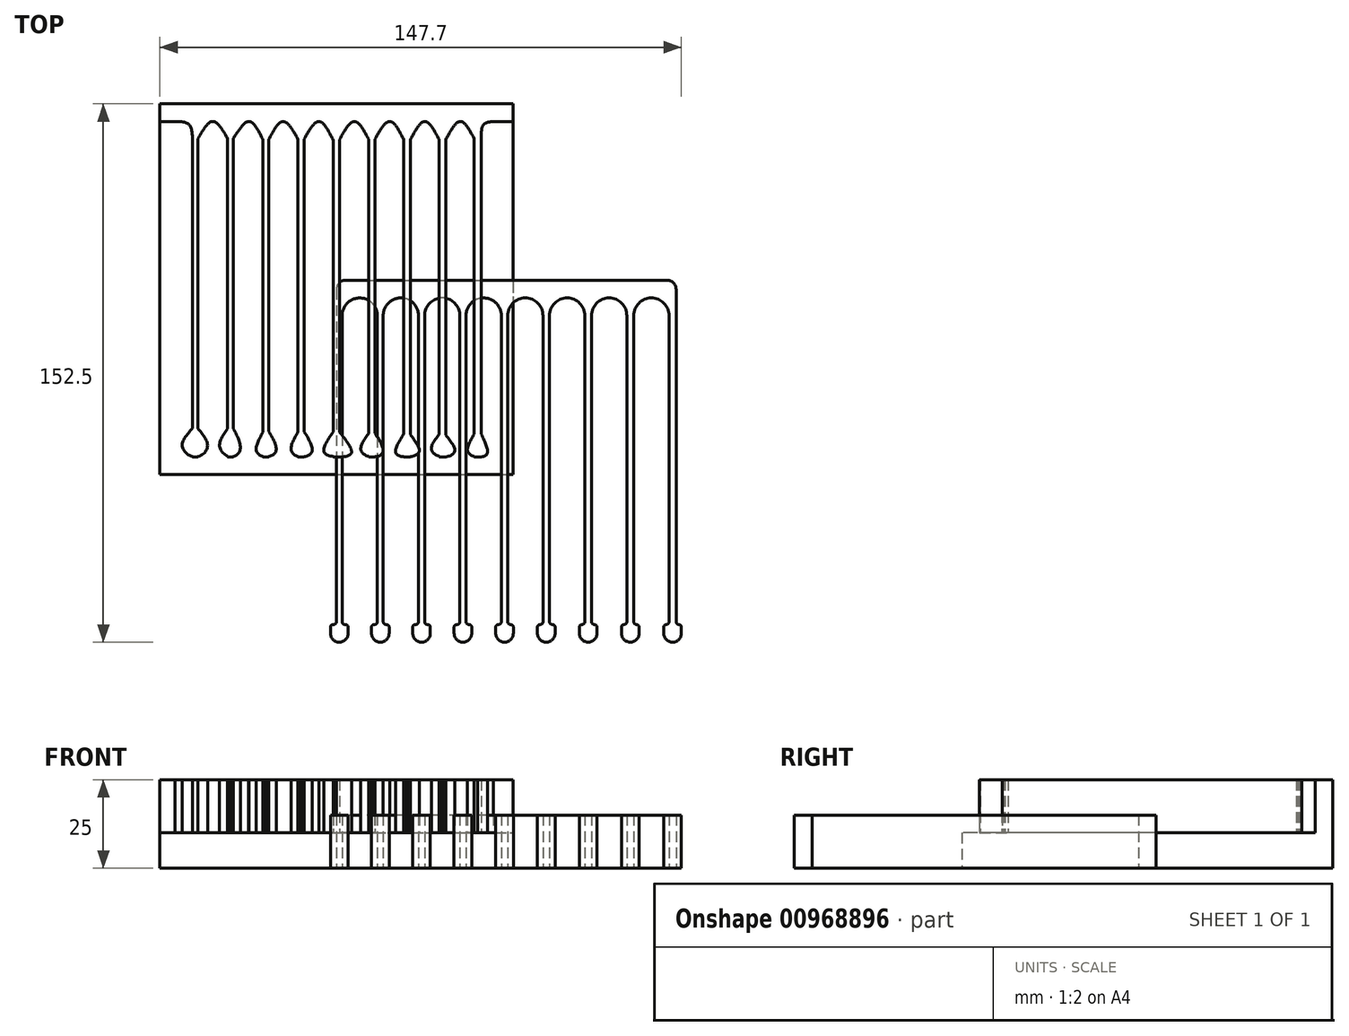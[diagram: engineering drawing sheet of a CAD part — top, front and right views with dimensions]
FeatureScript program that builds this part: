
annotation { "Feature Type Name" : "Feature", "Feature Type Description" : "" }
export const myFeature = defineFeature(function(context is Context, id is Id, definition is map)
    precondition{}
    {
        {
            var Q0;
            Q0=qCreatedBy(makeId("Top.planeOp"),FACE);
            var sketch = newSketch(context, id + "F0", { "sketchPlane" : qUnion([Q0])});
            skLineSegment(sketch, "E0.bottom", {"start": v(-50, 50) * mm, "end": v(50, 50) * mm});
            skLineSegment(sketch, "E0.top", {"start": v(-50, -50) * mm, "end": v(50, -50) * mm});
            skPoint(sketch, "E0.middle", {"position": v(0, 0) * mm});
            skLineSegment(sketch, "E1", {"start": v(-131.96, 0) * mm, "end": v(145.8, 0) * mm});
            skLineSegment(sketch, "E2.bottom", {"start": v(-0.9, 50) * mm, "end": v(0.9, 50) * mm});
            skLineSegment(sketch, "E2.top", {"start": v(-0.9, -50) * mm, "end": v(0.9, -50) * mm});
            skLineSegment(sketch, "E2.left", {"start": v(-0.9, 50) * mm, "end": v(-0.9, -50) * mm});
            skLineSegment(sketch, "E2.right", {"start": v(0.9, 50) * mm, "end": v(0.9, -50) * mm});
            skLineSegment(sketch, "E3", {"start": v(0, 0) * mm, "end": v(10, 0) * mm});
            skLineSegment(sketch, "E4", {"start": v(10, 0) * mm, "end": v(20, 0) * mm});
            skLineSegment(sketch, "E5", {"start": v(20, 0) * mm, "end": v(30, 0) * mm});
            skLineSegment(sketch, "E6", {"start": v(30, 0) * mm, "end": v(40, 0) * mm});
            skLineSegment(sketch, "E7", {"start": v(0, 86.17) * mm, "end": v(0, -73.16) * mm});
            skLineSegment(sketch, "E8.bottom", {"start": v(9.08, 50) * mm, "end": v(10.93, 50) * mm});
            skLineSegment(sketch, "E8.top", {"start": v(9.08, -50) * mm, "end": v(10.93, -50) * mm});
            skLineSegment(sketch, "E8.left", {"start": v(9.08, 50) * mm, "end": v(9.08, -50) * mm});
            skLineSegment(sketch, "E8.right", {"start": v(10.93, 50) * mm, "end": v(10.93, -50) * mm});
            skPoint(sketch, "E8.middle", {"position": v(10, 0) * mm});
            skLineSegment(sketch, "E9.bottom", {"start": v(19.05, 50) * mm, "end": v(20.95, 50) * mm});
            skLineSegment(sketch, "E9.top", {"start": v(19.05, -50) * mm, "end": v(20.95, -50) * mm});
            skLineSegment(sketch, "E9.left", {"start": v(19.05, 50) * mm, "end": v(19.05, -50) * mm});
            skLineSegment(sketch, "E9.right", {"start": v(20.95, 50) * mm, "end": v(20.95, -50) * mm});
            skPoint(sketch, "E9.middle", {"position": v(20, 0) * mm});
            skLineSegment(sketch, "E10.bottom", {"start": v(29.02, 50) * mm, "end": v(30.97, 50) * mm});
            skLineSegment(sketch, "E10.top", {"start": v(29.02, -50) * mm, "end": v(30.97, -50) * mm});
            skLineSegment(sketch, "E10.left", {"start": v(29.02, 50) * mm, "end": v(29.02, -50) * mm});
            skLineSegment(sketch, "E10.right", {"start": v(30.97, 50) * mm, "end": v(30.97, -50) * mm});
            skPoint(sketch, "E10.middle", {"position": v(30, 0) * mm});
            skLineSegment(sketch, "E11.bottom", {"start": v(39, 50) * mm, "end": v(41, 50) * mm});
            skLineSegment(sketch, "E11.top", {"start": v(39, -50) * mm, "end": v(41, -50) * mm});
            skLineSegment(sketch, "E11.left", {"start": v(39, 50) * mm, "end": v(39, -50) * mm});
            skLineSegment(sketch, "E11.right", {"start": v(41, 50) * mm, "end": v(41, -50) * mm});
            skPoint(sketch, "E11.middle", {"position": v(40, 0) * mm});
            skLineSegment(sketch, "E12", {"start": v(0, 0) * mm, "end": v(-10, 0) * mm});
            skLineSegment(sketch, "E13", {"start": v(-10, 0) * mm, "end": v(-20, 0) * mm});
            skLineSegment(sketch, "E14", {"start": v(-20, 0) * mm, "end": v(-30, 0) * mm});
            skLineSegment(sketch, "E15", {"start": v(-30, 0) * mm, "end": v(-40, 0) * mm});
            skLineSegment(sketch, "E16.bottom", {"start": v(-10.88, 50) * mm, "end": v(-9.13, 50) * mm});
            skLineSegment(sketch, "E16.top", {"start": v(-10.88, -50) * mm, "end": v(-9.13, -50) * mm});
            skLineSegment(sketch, "E16.left", {"start": v(-10.88, 50) * mm, "end": v(-10.88, -50) * mm});
            skLineSegment(sketch, "E16.right", {"start": v(-9.13, 50) * mm, "end": v(-9.13, -50) * mm});
            skPoint(sketch, "E16.middle", {"position": v(-10, 0) * mm});
            skLineSegment(sketch, "E17.bottom", {"start": v(-20.85, 50) * mm, "end": v(-19.15, 50) * mm});
            skLineSegment(sketch, "E17.top", {"start": v(-20.85, -50) * mm, "end": v(-19.15, -50) * mm});
            skLineSegment(sketch, "E17.left", {"start": v(-20.85, 50) * mm, "end": v(-20.85, -50) * mm});
            skLineSegment(sketch, "E17.right", {"start": v(-19.15, 50) * mm, "end": v(-19.15, -50) * mm});
            skPoint(sketch, "E17.middle", {"position": v(-20, 0) * mm});
            skLineSegment(sketch, "E18.bottom", {"start": v(-30.83, 50) * mm, "end": v(-29.18, 50) * mm});
            skLineSegment(sketch, "E18.top", {"start": v(-30.83, -50) * mm, "end": v(-29.18, -50) * mm});
            skLineSegment(sketch, "E18.left", {"start": v(-30.83, 50) * mm, "end": v(-30.83, -50) * mm});
            skLineSegment(sketch, "E18.right", {"start": v(-29.18, 50) * mm, "end": v(-29.18, -50) * mm});
            skPoint(sketch, "E18.middle", {"position": v(-30, 0) * mm});
            skLineSegment(sketch, "E19.bottom", {"start": v(-40.8, 50) * mm, "end": v(-39.2, 50) * mm});
            skLineSegment(sketch, "E19.top", {"start": v(-40.8, -50) * mm, "end": v(-39.2, -50) * mm});
            skLineSegment(sketch, "E19.left", {"start": v(-40.8, 50) * mm, "end": v(-40.8, -50) * mm});
            skLineSegment(sketch, "E19.right", {"start": v(-39.2, 50) * mm, "end": v(-39.2, -50) * mm});
            skPoint(sketch, "E19.middle", {"position": v(-40, 0) * mm});
            skLineSegment(sketch, "E20", {"start": v(40, 0) * mm, "end": v(50, 0) * mm});
            skLineSegment(sketch, "E21", {"start": v(-40, 0) * mm, "end": v(-50, 0) * mm});
            skLineSegment(sketch, "E22", {"start": v(-50, 50) * mm, "end": v(-50, -50) * mm});
            skLineSegment(sketch, "E23", {"start": v(50, 50) * mm, "end": v(50, -50) * mm});
            skPoint(sketch, "E24.orphan", {"position": v(100, 50) * mm});
            skPoint(sketch, "E25.orphan", {"position": v(100, -50) * mm});
            skPoint(sketch, "E26.orphan", {"position": v(-100, -50) * mm});
            skPoint(sketch, "E27.orphan", {"position": v(-100, 50) * mm});
            skLineSegment(sketch, "E28", {"start": v(-50, 50) * mm, "end": v(-50, 45) * mm});
            skLineSegment(sketch, "E29", {"start": v(-50, 45) * mm, "end": v(50, 45) * mm});
            skFitSpline(sketch, "E30", {"points": [v(-39.2, 40.14) * mm, v(-35.05, 45) * mm, v(-30.83, 40.15) * mm], "startDerivative": vector(8.28, 14.59) * mm, "endDerivative": vector(8.47, -14.54) * mm});
            skFitSpline(sketch, "E31", {"points": [v(-29.18, 40.2) * mm, v(-24.72, 45) * mm, v(-20.85, 39.83) * mm], "startDerivative": vector(9.17, 14.56) * mm, "endDerivative": vector(7.48, -15.35) * mm});
            skFitSpline(sketch, "E32", {"points": [v(-19.15, 39.93) * mm, v(-15.11, 45) * mm, v(-10.88, 39.9) * mm], "startDerivative": vector(8.05, 15.26) * mm, "endDerivative": vector(8.5, -15.27) * mm});
            skFitSpline(sketch, "E33", {"points": [v(-9.13, 40.03) * mm, v(-4.96, 45) * mm, v(-0.9, 39.67) * mm], "startDerivative": vector(8.48, 15.14) * mm, "endDerivative": vector(7.98, -15.77) * mm});
            skFitSpline(sketch, "E34", {"points": [v(0.9, 39.88) * mm, v(5.1, 45) * mm, v(9.08, 40) * mm], "startDerivative": vector(8.4, 15.25) * mm, "endDerivative": vector(7.96, -15.1) * mm});
            skFitSpline(sketch, "E35", {"points": [v(10.93, 40.04) * mm, v(15.1, 45) * mm, v(19.05, 39.86) * mm], "startDerivative": vector(8.49, 14.96) * mm, "endDerivative": vector(7.76, -15.32) * mm});
            skFitSpline(sketch, "E36", {"points": [v(20.95, 39.83) * mm, v(25.05, 45) * mm, v(29.02, 39.93) * mm], "startDerivative": vector(8.18, 15.43) * mm, "endDerivative": vector(7.97, -15.3) * mm});
            skFitSpline(sketch, "E37", {"points": [v(30.97, 39.85) * mm, v(35.1, 45) * mm, v(39, 40.14) * mm], "startDerivative": vector(8.18, 15.23) * mm, "endDerivative": vector(7.87, -14.8) * mm});
            skFitSpline(sketch, "E38", {"points": [v(-45.79, 45) * mm, v(-41.8, 44.16) * mm, v(-40.8, 40.58) * mm], "startDerivative": vector(9.28, -0.19) * mm, "endDerivative": vector(0.63, -8.72) * mm});
            skFitSpline(sketch, "E39", {"points": [v(41, 40.1) * mm, v(41.67, 44.1) * mm, v(44.48, 45) * mm], "startDerivative": vector(-0.07, 8.9) * mm, "endDerivative": vector(7.22, 0.69) * mm});
            skFitSpline(sketch, "E40", {"points": [v(-40.8, -41.94) * mm, v(-43.65, -47.12) * mm, v(-40, -50) * mm, v(-36.55, -47.26) * mm, v(-39.2, -42.01) * mm], "startDerivative": vector(-17.63, -19.78) * mm, "endDerivative": vector(-16.6, 20.3) * mm});
            skFitSpline(sketch, "E41", {"points": [v(-30.83, -42.01) * mm, v(-33.07, -47.2) * mm, v(-30, -50) * mm, v(-27.32, -48.12) * mm, v(-29.18, -42.01) * mm], "startDerivative": vector(-14.12, -19.61) * mm, "endDerivative": vector(-11.98, 23.35) * mm});
            skFitSpline(sketch, "E42", {"points": [v(-20.85, -43.08) * mm, v(-22.64, -48.4) * mm, v(-20, -50) * mm, v(-17.17, -48.47) * mm, v(-19.15, -42.8) * mm], "startDerivative": vector(-11.66, -21.24) * mm, "endDerivative": vector(-12.59, 22.12) * mm});
            skFitSpline(sketch, "E43", {"points": [v(-10.88, -42.86) * mm, v(-12.77, -48.33) * mm, v(-10, -50) * mm, v(-6.95, -48.61) * mm, v(-9.13, -42.93) * mm], "startDerivative": vector(-12.25, -21.86) * mm, "endDerivative": vector(-13.83, 22.6) * mm});
            skFitSpline(sketch, "E44", {"points": [v(-0.9, -42.92) * mm, v(-3.55, -48.54) * mm, v(0, -50) * mm, v(4.18, -49) * mm, v(0.9, -43.02) * mm], "startDerivative": vector(-16.86, -24.11) * mm, "endDerivative": vector(-20.02, 25.12) * mm});
            skFitSpline(sketch, "E45", {"points": [v(9.08, -43.42) * mm, v(6.94, -48.19) * mm, v(10, -50) * mm, v(13.16, -48.7) * mm, v(10.93, -43.32) * mm], "startDerivative": vector(-13.73, -19.48) * mm, "endDerivative": vector(-14.17, 21.68) * mm});
            skFitSpline(sketch, "E46", {"points": [v(19.05, -43.47) * mm, v(16.83, -48.94) * mm, v(20, -50) * mm, v(23.4, -48.7) * mm, v(20.95, -43.67) * mm], "startDerivative": vector(-14.18, -22.89) * mm, "endDerivative": vector(-15.57, 21.12) * mm});
            skFitSpline(sketch, "E47", {"points": [v(29.02, -43.67) * mm, v(26.91, -47.99) * mm, v(30, -50) * mm, v(33.44, -48.6) * mm, v(30.97, -43.77) * mm], "startDerivative": vector(-13.65, -17.73) * mm, "endDerivative": vector(-15.5, 19.57) * mm});
            skFitSpline(sketch, "E48", {"points": [v(39, -43.57) * mm, v(37.2, -48.54) * mm, v(40, -50) * mm, v(42.67, -49.14) * mm, v(41, -43.57) * mm], "startDerivative": vector(-11.82, -20.28) * mm, "endDerivative": vector(-11.16, 22.74) * mm});
            skLineSegment(sketch, "E49.bottom", {"start": v(50, -50) * mm, "end": v(-50, -50) * mm});
            skLineSegment(sketch, "E49.top", {"start": v(50, -55) * mm, "end": v(-50, -55) * mm});
            skLineSegment(sketch, "E49.left", {"start": v(50, -50) * mm, "end": v(50, -55) * mm});
            skLineSegment(sketch, "E49.right", {"start": v(-50, -50) * mm, "end": v(-50, -55) * mm});
            skSolve(sketch);
        }
        {
            var Q0;
            {var subQ4=sQuery(id+"F0.wireOp",EDGE,"E22");var subQ5=sQuery(id+"F0.wireOp",EDGE,"E0.bottom");var subQ6=makeQuery(id+"F0.imprint","INTERSECT",VERTEX,{"derivedFrom":[subQ5,subQ4]});Q0=makeQuery(id+"F0.imprint","IMPRINT",FACE,{"disambiguationData":[TD([[makeQuery(id+"F0.imprint","IMPRINT",EDGE,{"disambiguationData":[TD([[subQ6,-1.0]])],"derivedFrom":subQ5}),-1.0]])]});}
            var Q1;
            {var subQ0=sQuery(id+"F0.wireOp",EDGE,"E11.right");var subQ1=sQuery(id+"F0.wireOp",EDGE,"E0.bottom");var subQ2=makeQuery(id+"F0.imprint","INTERSECT",VERTEX,{"derivedFrom":[subQ1,subQ0]});Q1=makeQuery(id+"F0.imprint","IMPRINT",FACE,{"disambiguationData":[TD([[makeQuery(id+"F0.imprint","IMPRINT",EDGE,{"disambiguationData":[TD([[subQ2,1.0]])],"derivedFrom":subQ1}),-1.0]])]});}
            var Q2;
            {var subQ4=sQuery(id+"F0.wireOp",EDGE,"E0.bottom");var subQ6=sQuery(id+"F0.wireOp",EDGE,"E11.left");var subQ7=makeQuery(id+"F0.imprint","INTERSECT",VERTEX,{"derivedFrom":[subQ4,subQ6]});Q2=makeQuery(id+"F0.imprint","IMPRINT",FACE,{"disambiguationData":[TD([[makeQuery(id+"F0.imprint","IMPRINT",EDGE,{"disambiguationData":[TD([[subQ7,1.0]])],"derivedFrom":subQ4}),-1.0]])]});}
            var Q3;
            {var subQ0=sQuery(id+"F0.wireOp",EDGE,"E2.left");var subQ1=sQuery(id+"F0.wireOp",EDGE,"E0.bottom");var subQ2=makeQuery(id+"F0.imprint","INTERSECT",VERTEX,{"derivedFrom":[subQ1,subQ0]});Q3=makeQuery(id+"F0.imprint","IMPRINT",FACE,{"disambiguationData":[TD([[makeQuery(id+"F0.imprint","IMPRINT",EDGE,{"disambiguationData":[TD([[subQ2,-1.0]])],"derivedFrom":subQ1}),-1.0]])]});}
            var Q4;
            {var subQ0=sQuery(id+"F0.wireOp",EDGE,"E8.left");var subQ1=sQuery(id+"F0.wireOp",EDGE,"E0.bottom");var subQ2=makeQuery(id+"F0.imprint","INTERSECT",VERTEX,{"derivedFrom":[subQ1,subQ0]});Q4=makeQuery(id+"F0.imprint","IMPRINT",FACE,{"disambiguationData":[TD([[makeQuery(id+"F0.imprint","IMPRINT",EDGE,{"disambiguationData":[TD([[subQ2,-1.0]])],"derivedFrom":subQ1}),-1.0]])]});}
            var Q5;
            {var subQ0=sQuery(id+"F0.wireOp",EDGE,"E10.left");var subQ1=sQuery(id+"F0.wireOp",EDGE,"E0.bottom");var subQ2=makeQuery(id+"F0.imprint","INTERSECT",VERTEX,{"derivedFrom":[subQ1,subQ0]});Q5=makeQuery(id+"F0.imprint","IMPRINT",FACE,{"disambiguationData":[TD([[makeQuery(id+"F0.imprint","IMPRINT",EDGE,{"disambiguationData":[TD([[subQ2,-1.0]])],"derivedFrom":subQ1}),-1.0]])]});}
            var Q6;
            {var subQ1=sQuery(id+"F0.wireOp",EDGE,"E0.bottom");var subQ7=sQuery(id+"F0.wireOp",EDGE,"E17.left");var subQ8=makeQuery(id+"F0.imprint","INTERSECT",VERTEX,{"derivedFrom":[subQ1,subQ7]});Q6=makeQuery(id+"F0.imprint","IMPRINT",FACE,{"disambiguationData":[TD([[makeQuery(id+"F0.imprint","IMPRINT",EDGE,{"disambiguationData":[TD([[subQ8,1.0]])],"derivedFrom":subQ1}),-1.0]])]});}
            var Q7;
            {var subQ0=sQuery(id+"F0.wireOp",EDGE,"E16.left");var subQ1=sQuery(id+"F0.wireOp",EDGE,"E0.bottom");var subQ2=makeQuery(id+"F0.imprint","INTERSECT",VERTEX,{"derivedFrom":[subQ1,subQ0]});Q7=makeQuery(id+"F0.imprint","IMPRINT",FACE,{"disambiguationData":[TD([[makeQuery(id+"F0.imprint","IMPRINT",EDGE,{"disambiguationData":[TD([[subQ2,1.0]])],"derivedFrom":subQ1}),-1.0]])]});}
            var Q8;
            {var subQ3=sQuery(id+"F0.wireOp",EDGE,"E18.left");var subQ5=sQuery(id+"F0.wireOp",EDGE,"E0.bottom");var subQ6=makeQuery(id+"F0.imprint","INTERSECT",VERTEX,{"derivedFrom":[subQ5,subQ3]});Q8=makeQuery(id+"F0.imprint","IMPRINT",FACE,{"disambiguationData":[TD([[makeQuery(id+"F0.imprint","IMPRINT",EDGE,{"disambiguationData":[TD([[subQ6,1.0]])],"derivedFrom":subQ5}),-1.0]])]});}
            var Q9;
            {var subQ0=sQuery(id+"F0.wireOp",EDGE,"E9.left");var subQ1=sQuery(id+"F0.wireOp",EDGE,"E0.bottom");var subQ2=makeQuery(id+"F0.imprint","INTERSECT",VERTEX,{"derivedFrom":[subQ1,subQ0]});Q9=makeQuery(id+"F0.imprint","IMPRINT",FACE,{"disambiguationData":[TD([[makeQuery(id+"F0.imprint","IMPRINT",EDGE,{"disambiguationData":[TD([[subQ2,-1.0]])],"derivedFrom":subQ1}),-1.0]])]});}
            var Q10;
            {var subQ1=sQuery(id+"F0.wireOp",EDGE,"E2.right");var subQ6=sQuery(id+"F0.wireOp",EDGE,"E0.bottom");var subQ9=makeQuery(id+"F0.imprint","INTERSECT",VERTEX,{"derivedFrom":[subQ6,subQ1]});Q10=makeQuery(id+"F0.imprint","IMPRINT",FACE,{"disambiguationData":[TD([[makeQuery(id+"F0.imprint","IMPRINT",EDGE,{"disambiguationData":[TD([[subQ9,-1.0]])],"derivedFrom":subQ6}),-1.0]])]});}
            var Q11;
            {var subQ0=sQuery(id+"F0.wireOp",EDGE,"E16.left");var subQ1=sQuery(id+"F0.wireOp",EDGE,"E0.bottom");var subQ2=makeQuery(id+"F0.imprint","INTERSECT",VERTEX,{"derivedFrom":[subQ1,subQ0]});Q11=makeQuery(id+"F0.imprint","IMPRINT",FACE,{"disambiguationData":[TD([[makeQuery(id+"F0.imprint","IMPRINT",EDGE,{"disambiguationData":[TD([[subQ2,-1.0]])],"derivedFrom":subQ1}),-1.0]])]});}
            var Q12;
            {var subQ1=sQuery(id+"F0.wireOp",EDGE,"E16.right");var subQ5=sQuery(id+"F0.wireOp",EDGE,"E0.bottom");var subQ6=makeQuery(id+"F0.imprint","INTERSECT",VERTEX,{"derivedFrom":[subQ5,subQ1]});Q12=makeQuery(id+"F0.imprint","IMPRINT",FACE,{"disambiguationData":[TD([[makeQuery(id+"F0.imprint","IMPRINT",EDGE,{"disambiguationData":[TD([[subQ6,-1.0]])],"derivedFrom":subQ5}),-1.0]])]});}
            var Q13;
            {var subQ4=sQuery(id+"F0.wireOp",EDGE,"E10.left");var subQ5=sQuery(id+"F0.wireOp",EDGE,"E0.bottom");var subQ6=makeQuery(id+"F0.imprint","INTERSECT",VERTEX,{"derivedFrom":[subQ5,subQ4]});Q13=makeQuery(id+"F0.imprint","IMPRINT",FACE,{"disambiguationData":[TD([[makeQuery(id+"F0.imprint","IMPRINT",EDGE,{"disambiguationData":[TD([[subQ6,1.0]])],"derivedFrom":subQ5}),-1.0]])]});}
            var Q14;
            {var subQ1=sQuery(id+"F0.wireOp",EDGE,"E23");var subQ3=sQuery(id+"F0.wireOp",EDGE,"E0.bottom");var subQ4=makeQuery(id+"F0.imprint","INTERSECT",VERTEX,{"derivedFrom":[subQ3,subQ1]});Q14=makeQuery(id+"F0.imprint","IMPRINT",FACE,{"disambiguationData":[TD([[makeQuery(id+"F0.imprint","IMPRINT",EDGE,{"disambiguationData":[TD([[subQ4,1.0]])],"derivedFrom":subQ3}),-1.0]])]});}
            var Q15;
            {var subQ0=sQuery(id+"F0.wireOp",EDGE,"E19.left");var subQ1=sQuery(id+"F0.wireOp",EDGE,"E0.bottom");var subQ2=makeQuery(id+"F0.imprint","INTERSECT",VERTEX,{"derivedFrom":[subQ1,subQ0]});Q15=makeQuery(id+"F0.imprint","IMPRINT",FACE,{"disambiguationData":[TD([[makeQuery(id+"F0.imprint","IMPRINT",EDGE,{"disambiguationData":[TD([[subQ2,-1.0]])],"derivedFrom":subQ1}),-1.0]])]});}
            var Q16;
            {var subQ5=sQuery(id+"F0.wireOp",EDGE,"E9.left");var subQ6=sQuery(id+"F0.wireOp",EDGE,"E0.bottom");var subQ7=makeQuery(id+"F0.imprint","INTERSECT",VERTEX,{"derivedFrom":[subQ6,subQ5]});Q16=makeQuery(id+"F0.imprint","IMPRINT",FACE,{"disambiguationData":[TD([[makeQuery(id+"F0.imprint","IMPRINT",EDGE,{"disambiguationData":[TD([[subQ7,1.0]])],"derivedFrom":subQ6}),-1.0]])]});}
            var Q17;
            {var subQ0=sQuery(id+"F0.wireOp",EDGE,"E2.right");var subQ1=sQuery(id+"F0.wireOp",EDGE,"E0.bottom");var subQ2=makeQuery(id+"F0.imprint","INTERSECT",VERTEX,{"derivedFrom":[subQ1,subQ0]});Q17=makeQuery(id+"F0.imprint","IMPRINT",FACE,{"disambiguationData":[TD([[makeQuery(id+"F0.imprint","IMPRINT",EDGE,{"disambiguationData":[TD([[subQ2,1.0]])],"derivedFrom":subQ1}),-1.0]])]});}
            var Q18;
            {var subQ0=sQuery(id+"F0.wireOp",EDGE,"E17.left");var subQ1=sQuery(id+"F0.wireOp",EDGE,"E0.bottom");var subQ2=makeQuery(id+"F0.imprint","INTERSECT",VERTEX,{"derivedFrom":[subQ1,subQ0]});Q18=makeQuery(id+"F0.imprint","IMPRINT",FACE,{"disambiguationData":[TD([[makeQuery(id+"F0.imprint","IMPRINT",EDGE,{"disambiguationData":[TD([[subQ2,-1.0]])],"derivedFrom":subQ1}),-1.0]])]});}
            var Q19;
            {var subQ0=sQuery(id+"F0.wireOp",EDGE,"E18.left");var subQ1=sQuery(id+"F0.wireOp",EDGE,"E0.bottom");var subQ2=makeQuery(id+"F0.imprint","INTERSECT",VERTEX,{"derivedFrom":[subQ1,subQ0]});Q19=makeQuery(id+"F0.imprint","IMPRINT",FACE,{"disambiguationData":[TD([[makeQuery(id+"F0.imprint","IMPRINT",EDGE,{"disambiguationData":[TD([[subQ2,-1.0]])],"derivedFrom":subQ1}),-1.0]])]});}
            var Q20;
            {var subQ0=sQuery(id+"F0.wireOp",EDGE,"E33");var subQ1=sQuery(id+"F0.wireOp",EDGE,"E29");var subQ2=makeQuery(id+"F0.imprint","INTERSECT",VERTEX,{"disambiguationData":[OD(0.0)],"derivedFrom":[subQ1,subQ0]});Q20=makeQuery(id+"F0.imprint","IMPRINT",FACE,{"disambiguationData":[TD([[makeQuery(id+"F0.imprint","IMPRINT",EDGE,{"disambiguationData":[TD([[subQ2,-1.0]])],"derivedFrom":subQ1}),1.0]])]});}
            var Q21;
            {var subQ0=sQuery(id+"F0.wireOp",EDGE,"E31");var subQ1=sQuery(id+"F0.wireOp",EDGE,"E29");var subQ2=makeQuery(id+"F0.imprint","INTERSECT",VERTEX,{"disambiguationData":[OD(0.0)],"derivedFrom":[subQ1,subQ0]});Q21=makeQuery(id+"F0.imprint","IMPRINT",FACE,{"disambiguationData":[TD([[makeQuery(id+"F0.imprint","IMPRINT",EDGE,{"disambiguationData":[TD([[subQ2,-1.0]])],"derivedFrom":subQ1}),1.0]])]});}
            var Q22;
            {var subQ0=sQuery(id+"F0.wireOp",EDGE,"E35");var subQ1=sQuery(id+"F0.wireOp",EDGE,"E29");var subQ2=makeQuery(id+"F0.imprint","INTERSECT",VERTEX,{"disambiguationData":[OD(0.0)],"derivedFrom":[subQ1,subQ0]});Q22=makeQuery(id+"F0.imprint","IMPRINT",FACE,{"disambiguationData":[TD([[makeQuery(id+"F0.imprint","IMPRINT",EDGE,{"disambiguationData":[TD([[subQ2,-1.0]])],"derivedFrom":subQ1}),1.0]])]});}
            var Q23;
            {var subQ0=sQuery(id+"F0.wireOp",EDGE,"E32");var subQ1=sQuery(id+"F0.wireOp",EDGE,"E17.right");var subQ2=makeQuery(id+"F0.imprint","INTERSECT",VERTEX,{"derivedFrom":[subQ1,subQ0]});Q23=makeQuery(id+"F0.imprint","IMPRINT",FACE,{"disambiguationData":[TD([[makeQuery(id+"F0.imprint","IMPRINT",EDGE,{"disambiguationData":[TD([[subQ2,1.0]])],"derivedFrom":subQ1}),1.0]])]});}
            var Q24;
            {var subQ0=sQuery(id+"F0.wireOp",EDGE,"E31");var subQ1=sQuery(id+"F0.wireOp",EDGE,"E18.right");var subQ2=makeQuery(id+"F0.imprint","INTERSECT",VERTEX,{"derivedFrom":[subQ1,subQ0]});Q24=makeQuery(id+"F0.imprint","IMPRINT",FACE,{"disambiguationData":[TD([[makeQuery(id+"F0.imprint","IMPRINT",EDGE,{"disambiguationData":[TD([[subQ2,1.0]])],"derivedFrom":subQ1}),1.0]])]});}
            var Q25;
            {var subQ0=sQuery(id+"F0.wireOp",EDGE,"E35");var subQ1=sQuery(id+"F0.wireOp",EDGE,"E9.left");var subQ2=makeQuery(id+"F0.imprint","INTERSECT",VERTEX,{"derivedFrom":[subQ1,subQ0]});Q25=makeQuery(id+"F0.imprint","IMPRINT",FACE,{"disambiguationData":[TD([[makeQuery(id+"F0.imprint","IMPRINT",EDGE,{"disambiguationData":[TD([[subQ2,1.0]])],"derivedFrom":subQ1}),-1.0]])]});}
            var Q26;
            {var subQ0=sQuery(id+"F0.wireOp",EDGE,"E30");var subQ1=sQuery(id+"F0.wireOp",EDGE,"E18.left");var subQ2=makeQuery(id+"F0.imprint","INTERSECT",VERTEX,{"derivedFrom":[subQ1,subQ0]});Q26=makeQuery(id+"F0.imprint","IMPRINT",FACE,{"disambiguationData":[TD([[makeQuery(id+"F0.imprint","IMPRINT",EDGE,{"disambiguationData":[TD([[subQ2,1.0]])],"derivedFrom":subQ1}),-1.0]])]});}
            var Q27;
            {var subQ0=sQuery(id+"F0.wireOp",EDGE,"E33");var subQ1=sQuery(id+"F0.wireOp",EDGE,"E2.left");var subQ2=makeQuery(id+"F0.imprint","INTERSECT",VERTEX,{"derivedFrom":[subQ1,subQ0]});Q27=makeQuery(id+"F0.imprint","IMPRINT",FACE,{"disambiguationData":[TD([[makeQuery(id+"F0.imprint","IMPRINT",EDGE,{"disambiguationData":[TD([[subQ2,1.0]])],"derivedFrom":subQ1}),-1.0]])]});}
            var Q28;
            {var subQ0=sQuery(id+"F0.wireOp",EDGE,"E37");var subQ1=sQuery(id+"F0.wireOp",EDGE,"E11.left");var subQ2=makeQuery(id+"F0.imprint","INTERSECT",VERTEX,{"derivedFrom":[subQ1,subQ0]});Q28=makeQuery(id+"F0.imprint","IMPRINT",FACE,{"disambiguationData":[TD([[makeQuery(id+"F0.imprint","IMPRINT",EDGE,{"disambiguationData":[TD([[subQ2,1.0]])],"derivedFrom":subQ1}),-1.0]])]});}
            var Q29;
            {var subQ0=sQuery(id+"F0.wireOp",EDGE,"E33");var subQ1=sQuery(id+"F0.wireOp",EDGE,"E16.right");var subQ2=makeQuery(id+"F0.imprint","INTERSECT",VERTEX,{"derivedFrom":[subQ1,subQ0]});Q29=makeQuery(id+"F0.imprint","IMPRINT",FACE,{"disambiguationData":[TD([[makeQuery(id+"F0.imprint","IMPRINT",EDGE,{"disambiguationData":[TD([[subQ2,1.0]])],"derivedFrom":subQ1}),1.0]])]});}
            var Q30;
            {var subQ0=sQuery(id+"F0.wireOp",EDGE,"E35");var subQ1=sQuery(id+"F0.wireOp",EDGE,"E8.right");var subQ2=makeQuery(id+"F0.imprint","INTERSECT",VERTEX,{"derivedFrom":[subQ1,subQ0]});Q30=makeQuery(id+"F0.imprint","IMPRINT",FACE,{"disambiguationData":[TD([[makeQuery(id+"F0.imprint","IMPRINT",EDGE,{"disambiguationData":[TD([[subQ2,1.0]])],"derivedFrom":subQ1}),1.0]])]});}
            var Q31;
            {var subQ0=sQuery(id+"F0.wireOp",EDGE,"E31");var subQ1=sQuery(id+"F0.wireOp",EDGE,"E17.left");var subQ2=makeQuery(id+"F0.imprint","INTERSECT",VERTEX,{"derivedFrom":[subQ1,subQ0]});Q31=makeQuery(id+"F0.imprint","IMPRINT",FACE,{"disambiguationData":[TD([[makeQuery(id+"F0.imprint","IMPRINT",EDGE,{"disambiguationData":[TD([[subQ2,1.0]])],"derivedFrom":subQ1}),-1.0]])]});}
            var Q32;
            {var subQ0=sQuery(id+"F0.wireOp",EDGE,"E29");var subQ1=sQuery(id+"F0.wireOp",EDGE,"E2.right");var subQ2=makeQuery(id+"F0.imprint","INTERSECT",VERTEX,{"derivedFrom":[subQ1,subQ0]});Q32=makeQuery(id+"F0.imprint","IMPRINT",FACE,{"disambiguationData":[TD([[makeQuery(id+"F0.imprint","IMPRINT",EDGE,{"disambiguationData":[TD([[subQ2,-1.0]])],"derivedFrom":subQ1}),1.0]])]});}
            var Q33;
            {var subQ0=sQuery(id+"F0.wireOp",EDGE,"E30");var subQ1=sQuery(id+"F0.wireOp",EDGE,"E19.right");var subQ2=makeQuery(id+"F0.imprint","INTERSECT",VERTEX,{"derivedFrom":[subQ1,subQ0]});Q33=makeQuery(id+"F0.imprint","IMPRINT",FACE,{"disambiguationData":[TD([[makeQuery(id+"F0.imprint","IMPRINT",EDGE,{"disambiguationData":[TD([[subQ2,1.0]])],"derivedFrom":subQ1}),1.0]])]});}
            var Q34;
            {var subQ0=sQuery(id+"F0.wireOp",EDGE,"E37");var subQ1=sQuery(id+"F0.wireOp",EDGE,"E10.right");var subQ2=makeQuery(id+"F0.imprint","INTERSECT",VERTEX,{"derivedFrom":[subQ1,subQ0]});Q34=makeQuery(id+"F0.imprint","IMPRINT",FACE,{"disambiguationData":[TD([[makeQuery(id+"F0.imprint","IMPRINT",EDGE,{"disambiguationData":[TD([[subQ2,1.0]])],"derivedFrom":subQ1}),1.0]])]});}
            var Q35;
            {var subQ0=sQuery(id+"F0.wireOp",EDGE,"E36");var subQ1=sQuery(id+"F0.wireOp",EDGE,"E10.left");var subQ2=makeQuery(id+"F0.imprint","INTERSECT",VERTEX,{"derivedFrom":[subQ1,subQ0]});Q35=makeQuery(id+"F0.imprint","IMPRINT",FACE,{"disambiguationData":[TD([[makeQuery(id+"F0.imprint","IMPRINT",EDGE,{"disambiguationData":[TD([[subQ2,1.0]])],"derivedFrom":subQ1}),-1.0]])]});}
            var Q36;
            {var subQ0=sQuery(id+"F0.wireOp",EDGE,"E36");var subQ1=sQuery(id+"F0.wireOp",EDGE,"E9.right");var subQ2=makeQuery(id+"F0.imprint","INTERSECT",VERTEX,{"derivedFrom":[subQ1,subQ0]});Q36=makeQuery(id+"F0.imprint","IMPRINT",FACE,{"disambiguationData":[TD([[makeQuery(id+"F0.imprint","IMPRINT",EDGE,{"disambiguationData":[TD([[subQ2,1.0]])],"derivedFrom":subQ1}),1.0]])]});}
            var Q37;
            {var subQ0=sQuery(id+"F0.wireOp",EDGE,"E32");var subQ1=sQuery(id+"F0.wireOp",EDGE,"E16.left");var subQ2=makeQuery(id+"F0.imprint","INTERSECT",VERTEX,{"derivedFrom":[subQ1,subQ0]});Q37=makeQuery(id+"F0.imprint","IMPRINT",FACE,{"disambiguationData":[TD([[makeQuery(id+"F0.imprint","IMPRINT",EDGE,{"disambiguationData":[TD([[subQ2,1.0]])],"derivedFrom":subQ1}),-1.0]])]});}
            var Q38;
            {var subQ0=sQuery(id+"F0.wireOp",EDGE,"E34");var subQ1=sQuery(id+"F0.wireOp",EDGE,"E8.left");var subQ2=makeQuery(id+"F0.imprint","INTERSECT",VERTEX,{"derivedFrom":[subQ1,subQ0]});Q38=makeQuery(id+"F0.imprint","IMPRINT",FACE,{"disambiguationData":[TD([[makeQuery(id+"F0.imprint","IMPRINT",EDGE,{"disambiguationData":[TD([[subQ2,1.0]])],"derivedFrom":subQ1}),-1.0]])]});}
            var Q39;
            {var subQ0=sQuery(id+"F0.wireOp",EDGE,"E29");var subQ1=sQuery(id+"F0.wireOp",EDGE,"E11.right");var subQ2=makeQuery(id+"F0.imprint","INTERSECT",VERTEX,{"derivedFrom":[subQ1,subQ0]});Q39=makeQuery(id+"F0.imprint","IMPRINT",FACE,{"disambiguationData":[TD([[makeQuery(id+"F0.imprint","IMPRINT",EDGE,{"disambiguationData":[TD([[subQ2,-1.0]])],"derivedFrom":subQ1}),1.0]])]});}
            var Q40;
            {var subQ0=sQuery(id+"F0.wireOp",EDGE,"E38");Q40=makeQuery(id+"F0.imprint","IMPRINT",FACE,{"disambiguationData":[TD([[makeQuery(id+"F0.imprint","IMPRINT",EDGE,{"derivedFrom":subQ0}),1.0]])]});}
            var Q41;
            {var subQ0=sQuery(id+"F0.wireOp",EDGE,"E39");var subQ1=sQuery(id+"F0.wireOp",EDGE,"E11.right");var subQ2=makeQuery(id+"F0.imprint","INTERSECT",VERTEX,{"disambiguationData":[OD(0.0)],"derivedFrom":[subQ1,subQ0]});Q41=makeQuery(id+"F0.imprint","IMPRINT",FACE,{"disambiguationData":[TD([[makeQuery(id+"F0.imprint","IMPRINT",EDGE,{"disambiguationData":[TD([[subQ2,1.0]])],"derivedFrom":subQ1}),-1.0]])]});}
            var Q42;
            {var subQ0=sQuery(id+"F0.wireOp",EDGE,"E44");var subQ1=sQuery(id+"F0.wireOp",EDGE,"E0.top");var subQ2=makeQuery(id+"F0.imprint","INTERSECT",VERTEX,{"derivedFrom":[subQ1,subQ0]});Q42=makeQuery(id+"F0.imprint","IMPRINT",FACE,{"disambiguationData":[TD([[makeQuery(id+"F0.imprint","IMPRINT",EDGE,{"disambiguationData":[TD([[subQ2,1.0]])],"derivedFrom":subQ1}),1.0]])]});}
            var Q43;
            {var subQ0=sQuery(id+"F0.wireOp",EDGE,"E43");var subQ1=sQuery(id+"F0.wireOp",EDGE,"E16.left");var subQ2=makeQuery(id+"F0.imprint","INTERSECT",VERTEX,{"disambiguationData":[OD(0.0)],"derivedFrom":[subQ1,subQ0]});Q43=makeQuery(id+"F0.imprint","IMPRINT",FACE,{"disambiguationData":[TD([[makeQuery(id+"F0.imprint","IMPRINT",EDGE,{"disambiguationData":[TD([[subQ2,-1.0]])],"derivedFrom":subQ1}),-1.0]])]});}
            var Q44;
            {var subQ1=sQuery(id+"F0.wireOp",EDGE,"E2.right");var subQ5=sQuery(id+"F0.wireOp",EDGE,"E1");var subQ6=makeQuery(id+"F0.imprint","INTERSECT",VERTEX,{"derivedFrom":[subQ5,subQ1]});Q44=makeQuery(id+"F0.imprint","IMPRINT",FACE,{"disambiguationData":[TD([[makeQuery(id+"F0.imprint","IMPRINT",EDGE,{"disambiguationData":[TD([[subQ6,1.0]])],"derivedFrom":subQ5}),-1.0]])]});}
            var Q45;
            {var subQ0=sQuery(id+"F0.wireOp",EDGE,"E42");var subQ1=sQuery(id+"F0.wireOp",EDGE,"E17.right");var subQ2=makeQuery(id+"F0.imprint","INTERSECT",VERTEX,{"disambiguationData":[OD(0.0)],"derivedFrom":[subQ1,subQ0]});Q45=makeQuery(id+"F0.imprint","IMPRINT",FACE,{"disambiguationData":[TD([[makeQuery(id+"F0.imprint","IMPRINT",EDGE,{"disambiguationData":[TD([[subQ2,-1.0]])],"derivedFrom":subQ1}),1.0]])]});}
            var Q46;
            {var subQ1=sQuery(id+"F0.wireOp",EDGE,"E1");var subQ3=makeQuery(id+"F0.imprint","IMPRINT",VERTEX,{"disambiguationData":[OD(6.0)],"derivedFrom":subQ1});Q46=makeQuery(id+"F0.imprint","IMPRINT",FACE,{"disambiguationData":[TD([[makeQuery(id+"F0.imprint","IMPRINT",EDGE,{"disambiguationData":[TD([[subQ3,1.0]])],"derivedFrom":subQ1}),-1.0]])]});}
            var Q47;
            {var subQ0=sQuery(id+"F0.wireOp",EDGE,"E40");var subQ1=sQuery(id+"F0.wireOp",EDGE,"E19.right");var subQ2=makeQuery(id+"F0.imprint","INTERSECT",VERTEX,{"disambiguationData":[OD(0.0)],"derivedFrom":[subQ1,subQ0]});Q47=makeQuery(id+"F0.imprint","IMPRINT",FACE,{"disambiguationData":[TD([[makeQuery(id+"F0.imprint","IMPRINT",EDGE,{"disambiguationData":[TD([[subQ2,-1.0]])],"derivedFrom":subQ1}),1.0]])]});}
            var Q48;
            {var subQ0=sQuery(id+"F0.wireOp",EDGE,"E47");var subQ1=sQuery(id+"F0.wireOp",EDGE,"E10.left");var subQ2=makeQuery(id+"F0.imprint","INTERSECT",VERTEX,{"disambiguationData":[OD(0.0)],"derivedFrom":[subQ1,subQ0]});Q48=makeQuery(id+"F0.imprint","IMPRINT",FACE,{"disambiguationData":[TD([[makeQuery(id+"F0.imprint","IMPRINT",EDGE,{"disambiguationData":[TD([[subQ2,-1.0]])],"derivedFrom":subQ1}),-1.0]])]});}
            var Q49;
            {var subQ0=sQuery(id+"F0.wireOp",EDGE,"E40");var subQ1=sQuery(id+"F0.wireOp",EDGE,"E19.left");var subQ2=makeQuery(id+"F0.imprint","INTERSECT",VERTEX,{"disambiguationData":[OD(0.0)],"derivedFrom":[subQ1,subQ0]});Q49=makeQuery(id+"F0.imprint","IMPRINT",FACE,{"disambiguationData":[TD([[makeQuery(id+"F0.imprint","IMPRINT",EDGE,{"disambiguationData":[TD([[subQ2,-1.0]])],"derivedFrom":subQ1}),-1.0]])]});}
            var Q50;
            {var subQ0=sQuery(id+"F0.wireOp",EDGE,"E1");var subQ1=makeQuery(id+"F0.imprint","IMPRINT",VERTEX,{"disambiguationData":[OD(0.0)],"derivedFrom":subQ0});Q50=makeQuery(id+"F0.imprint","IMPRINT",FACE,{"disambiguationData":[TD([[makeQuery(id+"F0.imprint","IMPRINT",EDGE,{"disambiguationData":[TD([[subQ1,-1.0]])],"derivedFrom":subQ0}),-1.0]])]});}
            var Q51;
            {var subQ0=sQuery(id+"F0.wireOp",EDGE,"E42");var subQ1=sQuery(id+"F0.wireOp",EDGE,"E17.left");var subQ2=makeQuery(id+"F0.imprint","INTERSECT",VERTEX,{"disambiguationData":[OD(0.0)],"derivedFrom":[subQ1,subQ0]});Q51=makeQuery(id+"F0.imprint","IMPRINT",FACE,{"disambiguationData":[TD([[makeQuery(id+"F0.imprint","IMPRINT",EDGE,{"disambiguationData":[TD([[subQ2,-1.0]])],"derivedFrom":subQ1}),-1.0]])]});}
            var Q52;
            {var subQ0=sQuery(id+"F0.wireOp",EDGE,"E44");var subQ1=sQuery(id+"F0.wireOp",EDGE,"E2.left");var subQ2=makeQuery(id+"F0.imprint","INTERSECT",VERTEX,{"disambiguationData":[OD(0.0)],"derivedFrom":[subQ1,subQ0]});Q52=makeQuery(id+"F0.imprint","IMPRINT",FACE,{"disambiguationData":[TD([[makeQuery(id+"F0.imprint","IMPRINT",EDGE,{"disambiguationData":[TD([[subQ2,-1.0]])],"derivedFrom":subQ1}),-1.0]])]});}
            var Q53;
            {var subQ0=sQuery(id+"F0.wireOp",EDGE,"E43");var subQ1=sQuery(id+"F0.wireOp",EDGE,"E16.right");var subQ2=makeQuery(id+"F0.imprint","INTERSECT",VERTEX,{"disambiguationData":[OD(0.0)],"derivedFrom":[subQ1,subQ0]});Q53=makeQuery(id+"F0.imprint","IMPRINT",FACE,{"disambiguationData":[TD([[makeQuery(id+"F0.imprint","IMPRINT",EDGE,{"disambiguationData":[TD([[subQ2,-1.0]])],"derivedFrom":subQ1}),1.0]])]});}
            var Q54;
            {var subQ1=sQuery(id+"F0.wireOp",EDGE,"E1");var subQ3=makeQuery(id+"F0.imprint","IMPRINT",VERTEX,{"disambiguationData":[OD(7.0)],"derivedFrom":subQ1});Q54=makeQuery(id+"F0.imprint","IMPRINT",FACE,{"disambiguationData":[TD([[makeQuery(id+"F0.imprint","IMPRINT",EDGE,{"disambiguationData":[TD([[subQ3,1.0]])],"derivedFrom":subQ1}),-1.0]])]});}
            var Q55;
            {var subQ0=sQuery(id+"F0.wireOp",EDGE,"E48");var subQ1=sQuery(id+"F0.wireOp",EDGE,"E11.left");var subQ2=makeQuery(id+"F0.imprint","INTERSECT",VERTEX,{"disambiguationData":[OD(0.0)],"derivedFrom":[subQ1,subQ0]});Q55=makeQuery(id+"F0.imprint","IMPRINT",FACE,{"disambiguationData":[TD([[makeQuery(id+"F0.imprint","IMPRINT",EDGE,{"disambiguationData":[TD([[subQ2,-1.0]])],"derivedFrom":subQ1}),-1.0]])]});}
            var Q56;
            {var subQ0=sQuery(id+"F0.wireOp",EDGE,"E45");var subQ1=sQuery(id+"F0.wireOp",EDGE,"E8.right");var subQ2=makeQuery(id+"F0.imprint","INTERSECT",VERTEX,{"disambiguationData":[OD(0.0)],"derivedFrom":[subQ1,subQ0]});Q56=makeQuery(id+"F0.imprint","IMPRINT",FACE,{"disambiguationData":[TD([[makeQuery(id+"F0.imprint","IMPRINT",EDGE,{"disambiguationData":[TD([[subQ2,-1.0]])],"derivedFrom":subQ1}),1.0]])]});}
            var Q57;
            {var subQ0=sQuery(id+"F0.wireOp",EDGE,"E48");var subQ1=sQuery(id+"F0.wireOp",EDGE,"E0.top");var subQ2=makeQuery(id+"F0.imprint","INTERSECT",VERTEX,{"disambiguationData":[OD(0.0)],"derivedFrom":[subQ1,subQ0]});Q57=makeQuery(id+"F0.imprint","IMPRINT",FACE,{"disambiguationData":[TD([[makeQuery(id+"F0.imprint","IMPRINT",EDGE,{"disambiguationData":[TD([[subQ2,1.0]])],"derivedFrom":subQ1}),1.0]])]});}
            var Q58;
            {var subQ0=sQuery(id+"F0.wireOp",EDGE,"E46");var subQ1=sQuery(id+"F0.wireOp",EDGE,"E9.left");var subQ2=makeQuery(id+"F0.imprint","INTERSECT",VERTEX,{"disambiguationData":[OD(0.0)],"derivedFrom":[subQ1,subQ0]});Q58=makeQuery(id+"F0.imprint","IMPRINT",FACE,{"disambiguationData":[TD([[makeQuery(id+"F0.imprint","IMPRINT",EDGE,{"disambiguationData":[TD([[subQ2,-1.0]])],"derivedFrom":subQ1}),-1.0]])]});}
            var Q59;
            {var subQ0=sQuery(id+"F0.wireOp",EDGE,"E47");var subQ1=sQuery(id+"F0.wireOp",EDGE,"E10.right");var subQ2=makeQuery(id+"F0.imprint","INTERSECT",VERTEX,{"disambiguationData":[OD(0.0)],"derivedFrom":[subQ1,subQ0]});Q59=makeQuery(id+"F0.imprint","IMPRINT",FACE,{"disambiguationData":[TD([[makeQuery(id+"F0.imprint","IMPRINT",EDGE,{"disambiguationData":[TD([[subQ2,-1.0]])],"derivedFrom":subQ1}),1.0]])]});}
            var Q60;
            {var subQ1=sQuery(id+"F0.wireOp",EDGE,"E1");var subQ3=makeQuery(id+"F0.imprint","IMPRINT",VERTEX,{"disambiguationData":[OD(3.0)],"derivedFrom":subQ1});Q60=makeQuery(id+"F0.imprint","IMPRINT",FACE,{"disambiguationData":[TD([[makeQuery(id+"F0.imprint","IMPRINT",EDGE,{"disambiguationData":[TD([[subQ3,1.0]])],"derivedFrom":subQ1}),-1.0]])]});}
            var Q61;
            {var subQ1=sQuery(id+"F0.wireOp",EDGE,"E1");var subQ3=makeQuery(id+"F0.imprint","IMPRINT",VERTEX,{"disambiguationData":[OD(1.0)],"derivedFrom":subQ1});Q61=makeQuery(id+"F0.imprint","IMPRINT",FACE,{"disambiguationData":[TD([[makeQuery(id+"F0.imprint","IMPRINT",EDGE,{"disambiguationData":[TD([[subQ3,-1.0]])],"derivedFrom":subQ1}),-1.0]])]});}
            var Q62;
            {var subQ0=sQuery(id+"F0.wireOp",EDGE,"E46");var subQ1=sQuery(id+"F0.wireOp",EDGE,"E9.right");var subQ2=makeQuery(id+"F0.imprint","INTERSECT",VERTEX,{"disambiguationData":[OD(0.0)],"derivedFrom":[subQ1,subQ0]});Q62=makeQuery(id+"F0.imprint","IMPRINT",FACE,{"disambiguationData":[TD([[makeQuery(id+"F0.imprint","IMPRINT",EDGE,{"disambiguationData":[TD([[subQ2,-1.0]])],"derivedFrom":subQ1}),1.0]])]});}
            var Q63;
            {var subQ0=sQuery(id+"F0.wireOp",EDGE,"E45");var subQ1=sQuery(id+"F0.wireOp",EDGE,"E8.left");var subQ2=makeQuery(id+"F0.imprint","INTERSECT",VERTEX,{"disambiguationData":[OD(0.0)],"derivedFrom":[subQ1,subQ0]});Q63=makeQuery(id+"F0.imprint","IMPRINT",FACE,{"disambiguationData":[TD([[makeQuery(id+"F0.imprint","IMPRINT",EDGE,{"disambiguationData":[TD([[subQ2,-1.0]])],"derivedFrom":subQ1}),-1.0]])]});}
            var Q64;
            {var subQ1=sQuery(id+"F0.wireOp",EDGE,"E1");var subQ3=makeQuery(id+"F0.imprint","IMPRINT",VERTEX,{"disambiguationData":[OD(4.0)],"derivedFrom":subQ1});Q64=makeQuery(id+"F0.imprint","IMPRINT",FACE,{"disambiguationData":[TD([[makeQuery(id+"F0.imprint","IMPRINT",EDGE,{"disambiguationData":[TD([[subQ3,1.0]])],"derivedFrom":subQ1}),-1.0]])]});}
            var Q65;
            {var subQ1=sQuery(id+"F0.wireOp",EDGE,"E1");var subQ3=makeQuery(id+"F0.imprint","IMPRINT",VERTEX,{"disambiguationData":[OD(5.0)],"derivedFrom":subQ1});Q65=makeQuery(id+"F0.imprint","IMPRINT",FACE,{"disambiguationData":[TD([[makeQuery(id+"F0.imprint","IMPRINT",EDGE,{"disambiguationData":[TD([[subQ3,-1.0]])],"derivedFrom":subQ1}),-1.0]])]});}
            var Q66;
            {var subQ0=sQuery(id+"F0.wireOp",EDGE,"E41");var subQ1=sQuery(id+"F0.wireOp",EDGE,"E18.right");var subQ2=makeQuery(id+"F0.imprint","INTERSECT",VERTEX,{"disambiguationData":[OD(0.0)],"derivedFrom":[subQ1,subQ0]});Q66=makeQuery(id+"F0.imprint","IMPRINT",FACE,{"disambiguationData":[TD([[makeQuery(id+"F0.imprint","IMPRINT",EDGE,{"disambiguationData":[TD([[subQ2,-1.0]])],"derivedFrom":subQ1}),1.0]])]});}
            var Q67;
            {var subQ0=sQuery(id+"F0.wireOp",EDGE,"E41");var subQ1=sQuery(id+"F0.wireOp",EDGE,"E18.left");var subQ2=makeQuery(id+"F0.imprint","INTERSECT",VERTEX,{"disambiguationData":[OD(0.0)],"derivedFrom":[subQ1,subQ0]});Q67=makeQuery(id+"F0.imprint","IMPRINT",FACE,{"disambiguationData":[TD([[makeQuery(id+"F0.imprint","IMPRINT",EDGE,{"disambiguationData":[TD([[subQ2,-1.0]])],"derivedFrom":subQ1}),-1.0]])]});}
            var Q68;
            {var subQ1=sQuery(id+"F0.wireOp",EDGE,"E1");var subQ3=makeQuery(id+"F0.imprint","IMPRINT",VERTEX,{"disambiguationData":[OD(2.0)],"derivedFrom":subQ1});Q68=makeQuery(id+"F0.imprint","IMPRINT",FACE,{"disambiguationData":[TD([[makeQuery(id+"F0.imprint","IMPRINT",EDGE,{"disambiguationData":[TD([[subQ3,-1.0]])],"derivedFrom":subQ1}),-1.0]])]});}
            var Q69;
            {var subQ1=sQuery(id+"F0.wireOp",EDGE,"E2.left");var subQ4=sQuery(id+"F0.wireOp",EDGE,"E1");var subQ5=makeQuery(id+"F0.imprint","INTERSECT",VERTEX,{"derivedFrom":[subQ4,subQ1]});Q69=makeQuery(id+"F0.imprint","IMPRINT",FACE,{"disambiguationData":[TD([[makeQuery(id+"F0.imprint","IMPRINT",EDGE,{"disambiguationData":[TD([[subQ5,-1.0]])],"derivedFrom":subQ4}),-1.0]])]});}
            var Q70;
            {var subQ0=sQuery(id+"F0.wireOp",EDGE,"E0.top");var subQ2=sQuery(id+"F0.wireOp",EDGE,"E44");var subQ4=makeQuery(id+"F0.imprint","INTERSECT",VERTEX,{"derivedFrom":[subQ0,subQ2]});Q70=makeQuery(id+"F0.imprint","IMPRINT",FACE,{"disambiguationData":[TD([[makeQuery(id+"F0.imprint","IMPRINT",EDGE,{"disambiguationData":[TD([[subQ4,1.0]])],"derivedFrom":subQ0}),-1.0]])]});}
            var Q71;
            {var subQ0=sQuery(id+"F0.wireOp",EDGE,"E16.right");var subQ1=sQuery(id+"F0.wireOp",EDGE,"E0.top");var subQ2=makeQuery(id+"F0.imprint","INTERSECT",VERTEX,{"derivedFrom":[subQ1,subQ0]});Q71=makeQuery(id+"F0.imprint","IMPRINT",FACE,{"disambiguationData":[TD([[makeQuery(id+"F0.imprint","IMPRINT",EDGE,{"disambiguationData":[TD([[subQ2,1.0]])],"derivedFrom":subQ1}),1.0]])]});}
            var Q72;
            {var subQ0=sQuery(id+"F0.wireOp",EDGE,"E19.left");var subQ1=sQuery(id+"F0.wireOp",EDGE,"E0.top");var subQ2=makeQuery(id+"F0.imprint","INTERSECT",VERTEX,{"derivedFrom":[subQ1,subQ0]});Q72=makeQuery(id+"F0.imprint","IMPRINT",FACE,{"disambiguationData":[TD([[makeQuery(id+"F0.imprint","IMPRINT",EDGE,{"disambiguationData":[TD([[subQ2,-1.0]])],"derivedFrom":subQ1}),1.0]])]});}
            var Q73;
            {var subQ0=sQuery(id+"F0.wireOp",EDGE,"E46");var subQ1=sQuery(id+"F0.wireOp",EDGE,"E0.top");var subQ2=makeQuery(id+"F0.imprint","INTERSECT",VERTEX,{"disambiguationData":[OD(0.0)],"derivedFrom":[subQ1,subQ0]});Q73=makeQuery(id+"F0.imprint","IMPRINT",FACE,{"disambiguationData":[TD([[makeQuery(id+"F0.imprint","IMPRINT",EDGE,{"disambiguationData":[TD([[subQ2,1.0]])],"derivedFrom":subQ1}),-1.0]])]});}
            var Q74;
            {var subQ0=sQuery(id+"F0.wireOp",EDGE,"E9.right");var subQ1=sQuery(id+"F0.wireOp",EDGE,"E0.top");var subQ2=makeQuery(id+"F0.imprint","INTERSECT",VERTEX,{"derivedFrom":[subQ1,subQ0]});Q74=makeQuery(id+"F0.imprint","IMPRINT",FACE,{"disambiguationData":[TD([[makeQuery(id+"F0.imprint","IMPRINT",EDGE,{"disambiguationData":[TD([[subQ2,1.0]])],"derivedFrom":subQ1}),1.0]])]});}
            var Q75;
            {var subQ0=sQuery(id+"F0.wireOp",EDGE,"E43");var subQ1=sQuery(id+"F0.wireOp",EDGE,"E0.top");var subQ2=makeQuery(id+"F0.imprint","INTERSECT",VERTEX,{"disambiguationData":[OD(0.0)],"derivedFrom":[subQ1,subQ0]});Q75=makeQuery(id+"F0.imprint","IMPRINT",FACE,{"disambiguationData":[TD([[makeQuery(id+"F0.imprint","IMPRINT",EDGE,{"disambiguationData":[TD([[subQ2,-1.0]])],"derivedFrom":subQ1}),-1.0]])]});}
            var Q76;
            {var subQ0=sQuery(id+"F0.wireOp",EDGE,"E45");var subQ1=sQuery(id+"F0.wireOp",EDGE,"E0.top");var subQ2=makeQuery(id+"F0.imprint","INTERSECT",VERTEX,{"disambiguationData":[OD(0.0)],"derivedFrom":[subQ1,subQ0]});Q76=makeQuery(id+"F0.imprint","IMPRINT",FACE,{"disambiguationData":[TD([[makeQuery(id+"F0.imprint","IMPRINT",EDGE,{"disambiguationData":[TD([[subQ2,-1.0]])],"derivedFrom":subQ1}),-1.0]])]});}
            var Q77;
            {var subQ0=sQuery(id+"F0.wireOp",EDGE,"E18.right");var subQ1=sQuery(id+"F0.wireOp",EDGE,"E0.top");var subQ2=makeQuery(id+"F0.imprint","INTERSECT",VERTEX,{"derivedFrom":[subQ1,subQ0]});Q77=makeQuery(id+"F0.imprint","IMPRINT",FACE,{"disambiguationData":[TD([[makeQuery(id+"F0.imprint","IMPRINT",EDGE,{"disambiguationData":[TD([[subQ2,1.0]])],"derivedFrom":subQ1}),1.0]])]});}
            var Q78;
            {var subQ0=sQuery(id+"F0.wireOp",EDGE,"E47");var subQ1=sQuery(id+"F0.wireOp",EDGE,"E0.top");var subQ2=makeQuery(id+"F0.imprint","INTERSECT",VERTEX,{"disambiguationData":[OD(0.0)],"derivedFrom":[subQ1,subQ0]});Q78=makeQuery(id+"F0.imprint","IMPRINT",FACE,{"disambiguationData":[TD([[makeQuery(id+"F0.imprint","IMPRINT",EDGE,{"disambiguationData":[TD([[subQ2,-1.0]])],"derivedFrom":subQ1}),-1.0]])]});}
            var Q79;
            {var subQ0=sQuery(id+"F0.wireOp",EDGE,"E41");var subQ1=sQuery(id+"F0.wireOp",EDGE,"E0.top");var subQ2=makeQuery(id+"F0.imprint","INTERSECT",VERTEX,{"disambiguationData":[OD(0.0)],"derivedFrom":[subQ1,subQ0]});Q79=makeQuery(id+"F0.imprint","IMPRINT",FACE,{"disambiguationData":[TD([[makeQuery(id+"F0.imprint","IMPRINT",EDGE,{"disambiguationData":[TD([[subQ2,-1.0]])],"derivedFrom":subQ1}),-1.0]])]});}
            var Q80;
            {var subQ0=sQuery(id+"F0.wireOp",EDGE,"E10.left");var subQ1=sQuery(id+"F0.wireOp",EDGE,"E0.top");var subQ2=makeQuery(id+"F0.imprint","INTERSECT",VERTEX,{"derivedFrom":[subQ1,subQ0]});Q80=makeQuery(id+"F0.imprint","IMPRINT",FACE,{"disambiguationData":[TD([[makeQuery(id+"F0.imprint","IMPRINT",EDGE,{"disambiguationData":[TD([[subQ2,-1.0]])],"derivedFrom":subQ1}),1.0]])]});}
            var Q81;
            {var subQ0=sQuery(id+"F0.wireOp",EDGE,"E8.left");var subQ1=sQuery(id+"F0.wireOp",EDGE,"E0.top");var subQ2=makeQuery(id+"F0.imprint","INTERSECT",VERTEX,{"derivedFrom":[subQ1,subQ0]});Q81=makeQuery(id+"F0.imprint","IMPRINT",FACE,{"disambiguationData":[TD([[makeQuery(id+"F0.imprint","IMPRINT",EDGE,{"disambiguationData":[TD([[subQ2,-1.0]])],"derivedFrom":subQ1}),1.0]])]});}
            var Q82;
            {var subQ0=sQuery(id+"F0.wireOp",EDGE,"E8.right");var subQ1=sQuery(id+"F0.wireOp",EDGE,"E0.top");var subQ2=makeQuery(id+"F0.imprint","INTERSECT",VERTEX,{"derivedFrom":[subQ1,subQ0]});Q82=makeQuery(id+"F0.imprint","IMPRINT",FACE,{"disambiguationData":[TD([[makeQuery(id+"F0.imprint","IMPRINT",EDGE,{"disambiguationData":[TD([[subQ2,1.0]])],"derivedFrom":subQ1}),1.0]])]});}
            var Q83;
            {var subQ0=sQuery(id+"F0.wireOp",EDGE,"E11.left");var subQ1=sQuery(id+"F0.wireOp",EDGE,"E0.top");var subQ2=makeQuery(id+"F0.imprint","INTERSECT",VERTEX,{"derivedFrom":[subQ1,subQ0]});Q83=makeQuery(id+"F0.imprint","IMPRINT",FACE,{"disambiguationData":[TD([[makeQuery(id+"F0.imprint","IMPRINT",EDGE,{"disambiguationData":[TD([[subQ2,-1.0]])],"derivedFrom":subQ1}),1.0]])]});}
            var Q84;
            {var subQ0=sQuery(id+"F0.wireOp",EDGE,"E40");var subQ1=sQuery(id+"F0.wireOp",EDGE,"E0.top");var subQ2=makeQuery(id+"F0.imprint","INTERSECT",VERTEX,{"disambiguationData":[OD(0.0)],"derivedFrom":[subQ1,subQ0]});Q84=makeQuery(id+"F0.imprint","IMPRINT",FACE,{"disambiguationData":[TD([[makeQuery(id+"F0.imprint","IMPRINT",EDGE,{"disambiguationData":[TD([[subQ2,-1.0]])],"derivedFrom":subQ1}),1.0]])]});}
            var Q85;
            {var subQ0=sQuery(id+"F0.wireOp",EDGE,"E48");var subQ1=sQuery(id+"F0.wireOp",EDGE,"E0.top");var subQ2=makeQuery(id+"F0.imprint","INTERSECT",VERTEX,{"disambiguationData":[OD(1.0)],"derivedFrom":[subQ1,subQ0]});Q85=makeQuery(id+"F0.imprint","IMPRINT",FACE,{"disambiguationData":[TD([[makeQuery(id+"F0.imprint","IMPRINT",EDGE,{"disambiguationData":[TD([[subQ2,-1.0]])],"derivedFrom":subQ1}),-1.0]])]});}
            var Q86;
            {var subQ0=sQuery(id+"F0.wireOp",EDGE,"E9.left");var subQ1=sQuery(id+"F0.wireOp",EDGE,"E0.top");var subQ2=makeQuery(id+"F0.imprint","INTERSECT",VERTEX,{"derivedFrom":[subQ1,subQ0]});Q86=makeQuery(id+"F0.imprint","IMPRINT",FACE,{"disambiguationData":[TD([[makeQuery(id+"F0.imprint","IMPRINT",EDGE,{"disambiguationData":[TD([[subQ2,-1.0]])],"derivedFrom":subQ1}),1.0]])]});}
            var Q87;
            {var subQ0=sQuery(id+"F0.wireOp",EDGE,"E16.left");var subQ1=sQuery(id+"F0.wireOp",EDGE,"E0.top");var subQ2=makeQuery(id+"F0.imprint","INTERSECT",VERTEX,{"derivedFrom":[subQ1,subQ0]});Q87=makeQuery(id+"F0.imprint","IMPRINT",FACE,{"disambiguationData":[TD([[makeQuery(id+"F0.imprint","IMPRINT",EDGE,{"disambiguationData":[TD([[subQ2,-1.0]])],"derivedFrom":subQ1}),1.0]])]});}
            var Q88;
            {var subQ0=sQuery(id+"F0.wireOp",EDGE,"E2.left");var subQ1=sQuery(id+"F0.wireOp",EDGE,"E0.top");var subQ2=makeQuery(id+"F0.imprint","INTERSECT",VERTEX,{"derivedFrom":[subQ1,subQ0]});Q88=makeQuery(id+"F0.imprint","IMPRINT",FACE,{"disambiguationData":[TD([[makeQuery(id+"F0.imprint","IMPRINT",EDGE,{"disambiguationData":[TD([[subQ2,1.0]])],"derivedFrom":subQ0}),1.0]])]});}
            var Q89;
            {var subQ0=sQuery(id+"F0.wireOp",EDGE,"E18.left");var subQ1=sQuery(id+"F0.wireOp",EDGE,"E0.top");var subQ2=makeQuery(id+"F0.imprint","INTERSECT",VERTEX,{"derivedFrom":[subQ1,subQ0]});Q89=makeQuery(id+"F0.imprint","IMPRINT",FACE,{"disambiguationData":[TD([[makeQuery(id+"F0.imprint","IMPRINT",EDGE,{"disambiguationData":[TD([[subQ2,-1.0]])],"derivedFrom":subQ1}),1.0]])]});}
            var Q90;
            {var subQ0=sQuery(id+"F0.wireOp",EDGE,"E42");var subQ1=sQuery(id+"F0.wireOp",EDGE,"E0.top");var subQ2=makeQuery(id+"F0.imprint","INTERSECT",VERTEX,{"disambiguationData":[OD(0.0)],"derivedFrom":[subQ1,subQ0]});Q90=makeQuery(id+"F0.imprint","IMPRINT",FACE,{"disambiguationData":[TD([[makeQuery(id+"F0.imprint","IMPRINT",EDGE,{"disambiguationData":[TD([[subQ2,-1.0]])],"derivedFrom":subQ1}),-1.0]])]});}
            var Q91;
            {var subQ0=sQuery(id+"F0.wireOp",EDGE,"E17.left");var subQ1=sQuery(id+"F0.wireOp",EDGE,"E0.top");var subQ2=makeQuery(id+"F0.imprint","INTERSECT",VERTEX,{"derivedFrom":[subQ1,subQ0]});Q91=makeQuery(id+"F0.imprint","IMPRINT",FACE,{"disambiguationData":[TD([[makeQuery(id+"F0.imprint","IMPRINT",EDGE,{"disambiguationData":[TD([[subQ2,-1.0]])],"derivedFrom":subQ1}),1.0]])]});}
            var Q92;
            {var subQ0=sQuery(id+"F0.wireOp",EDGE,"E10.right");var subQ1=sQuery(id+"F0.wireOp",EDGE,"E0.top");var subQ2=makeQuery(id+"F0.imprint","INTERSECT",VERTEX,{"derivedFrom":[subQ1,subQ0]});Q92=makeQuery(id+"F0.imprint","IMPRINT",FACE,{"disambiguationData":[TD([[makeQuery(id+"F0.imprint","IMPRINT",EDGE,{"disambiguationData":[TD([[subQ2,1.0]])],"derivedFrom":subQ1}),1.0]])]});}
            var Q93;
            {var subQ0=sQuery(id+"F0.wireOp",EDGE,"E17.right");var subQ1=sQuery(id+"F0.wireOp",EDGE,"E0.top");var subQ2=makeQuery(id+"F0.imprint","INTERSECT",VERTEX,{"derivedFrom":[subQ1,subQ0]});Q93=makeQuery(id+"F0.imprint","IMPRINT",FACE,{"disambiguationData":[TD([[makeQuery(id+"F0.imprint","IMPRINT",EDGE,{"disambiguationData":[TD([[subQ2,1.0]])],"derivedFrom":subQ1}),1.0]])]});}
            var Q94;
            {var subQ4=sQuery(id+"F0.wireOp",EDGE,"E1");var subQ8=makeQuery(id+"F0.imprint","IMPRINT",VERTEX,{"disambiguationData":[OD(0.0)],"derivedFrom":subQ4});Q94=makeQuery(id+"F0.imprint","IMPRINT",FACE,{"disambiguationData":[TD([[makeQuery(id+"F0.imprint","IMPRINT",EDGE,{"disambiguationData":[TD([[subQ8,-1.0]])],"derivedFrom":subQ4}),1.0]])]});}
            var Q95;
            {var subQ4=sQuery(id+"F0.wireOp",EDGE,"E1");var subQ9=makeQuery(id+"F0.imprint","IMPRINT",VERTEX,{"disambiguationData":[OD(7.0)],"derivedFrom":subQ4});Q95=makeQuery(id+"F0.imprint","IMPRINT",FACE,{"disambiguationData":[TD([[makeQuery(id+"F0.imprint","IMPRINT",EDGE,{"disambiguationData":[TD([[subQ9,1.0]])],"derivedFrom":subQ4}),1.0]])]});}
            var Q96;
            {var subQ4=sQuery(id+"F0.wireOp",EDGE,"E1");var subQ9=makeQuery(id+"F0.imprint","IMPRINT",VERTEX,{"disambiguationData":[OD(6.0)],"derivedFrom":subQ4});Q96=makeQuery(id+"F0.imprint","IMPRINT",FACE,{"disambiguationData":[TD([[makeQuery(id+"F0.imprint","IMPRINT",EDGE,{"disambiguationData":[TD([[subQ9,1.0]])],"derivedFrom":subQ4}),1.0]])]});}
            var Q97;
            {var subQ4=sQuery(id+"F0.wireOp",EDGE,"E1");var subQ8=makeQuery(id+"F0.imprint","IMPRINT",VERTEX,{"disambiguationData":[OD(5.0)],"derivedFrom":subQ4});Q97=makeQuery(id+"F0.imprint","IMPRINT",FACE,{"disambiguationData":[TD([[makeQuery(id+"F0.imprint","IMPRINT",EDGE,{"disambiguationData":[TD([[subQ8,-1.0]])],"derivedFrom":subQ4}),1.0]])]});}
            var Q98;
            {var subQ1=sQuery(id+"F0.wireOp",EDGE,"E1");var subQ5=sQuery(id+"F0.wireOp",EDGE,"E2.left");var subQ6=makeQuery(id+"F0.imprint","INTERSECT",VERTEX,{"derivedFrom":[subQ1,subQ5]});Q98=makeQuery(id+"F0.imprint","IMPRINT",FACE,{"disambiguationData":[TD([[makeQuery(id+"F0.imprint","IMPRINT",EDGE,{"disambiguationData":[TD([[subQ6,-1.0]])],"derivedFrom":subQ1}),1.0]])]});}
            var Q99;
            {var subQ1=sQuery(id+"F0.wireOp",EDGE,"E2.right");var subQ5=sQuery(id+"F0.wireOp",EDGE,"E1");var subQ8=makeQuery(id+"F0.imprint","INTERSECT",VERTEX,{"derivedFrom":[subQ5,subQ1]});Q99=makeQuery(id+"F0.imprint","IMPRINT",FACE,{"disambiguationData":[TD([[makeQuery(id+"F0.imprint","IMPRINT",EDGE,{"disambiguationData":[TD([[subQ8,1.0]])],"derivedFrom":subQ5}),1.0]])]});}
            var Q100;
            {var subQ4=sQuery(id+"F0.wireOp",EDGE,"E1");var subQ8=makeQuery(id+"F0.imprint","IMPRINT",VERTEX,{"disambiguationData":[OD(4.0)],"derivedFrom":subQ4});Q100=makeQuery(id+"F0.imprint","IMPRINT",FACE,{"disambiguationData":[TD([[makeQuery(id+"F0.imprint","IMPRINT",EDGE,{"disambiguationData":[TD([[subQ8,1.0]])],"derivedFrom":subQ4}),1.0]])]});}
            var Q101;
            {var subQ4=sQuery(id+"F0.wireOp",EDGE,"E1");var subQ6=makeQuery(id+"F0.imprint","IMPRINT",VERTEX,{"disambiguationData":[OD(2.0)],"derivedFrom":subQ4});Q101=makeQuery(id+"F0.imprint","IMPRINT",FACE,{"disambiguationData":[TD([[makeQuery(id+"F0.imprint","IMPRINT",EDGE,{"disambiguationData":[TD([[subQ6,-1.0]])],"derivedFrom":subQ4}),1.0]])]});}
            var Q102;
            {var subQ4=sQuery(id+"F0.wireOp",EDGE,"E1");var subQ6=makeQuery(id+"F0.imprint","IMPRINT",VERTEX,{"disambiguationData":[OD(1.0)],"derivedFrom":subQ4});Q102=makeQuery(id+"F0.imprint","IMPRINT",FACE,{"disambiguationData":[TD([[makeQuery(id+"F0.imprint","IMPRINT",EDGE,{"disambiguationData":[TD([[subQ6,-1.0]])],"derivedFrom":subQ4}),1.0]])]});}
            var Q103;
            {var subQ4=sQuery(id+"F0.wireOp",EDGE,"E1");var subQ8=makeQuery(id+"F0.imprint","IMPRINT",VERTEX,{"disambiguationData":[OD(3.0)],"derivedFrom":subQ4});Q103=makeQuery(id+"F0.imprint","IMPRINT",FACE,{"disambiguationData":[TD([[makeQuery(id+"F0.imprint","IMPRINT",EDGE,{"disambiguationData":[TD([[subQ8,1.0]])],"derivedFrom":subQ4}),1.0]])]});}
            extrude(context, id + "F1", {"entities" : qUnion([Q0, Q1, Q2, Q3, Q4, Q5, Q6, Q7, Q8, Q9, Q10, Q11, Q12, Q13, Q14, Q15, Q16, Q17, Q18, Q19, Q20, Q21, Q22, Q23, Q24, Q25, Q26, Q27, Q28, Q29, Q30, Q31, Q32, Q33, Q34, Q35, Q36, Q37, Q38, Q39, Q40, Q41, Q42, Q43, Q44, Q45, Q46, Q47, Q48, Q49, Q50, Q51, Q52, Q53, Q54, Q55, Q56, Q57, Q58, Q59, Q60, Q61, Q62, Q63, Q64, Q65, Q66, Q67, Q68, Q69, Q70, Q71, Q72, Q73, Q74, Q75, Q76, Q77, Q78, Q79, Q80, Q81, Q82, Q83, Q84, Q85, Q86, Q87, Q88, Q89, Q90, Q91, Q92, Q93, Q94, Q95, Q96, Q97, Q98, Q99, Q100, Q101, Q102, Q103]), "depth" : 25 * mm, "offsetDistance" : 25 * mm});
        }
        {
            var Q0;
            Q0=qCreatedBy(makeId("Top.planeOp"),FACE);
            var sketch = newSketch(context, id + "F2", { "sketchPlane" : qUnion([Q0])});
            skLineSegment(sketch, "E50.bottom", {"start": v(50, 50) * mm, "end": v(-50, 50) * mm});
            skLineSegment(sketch, "E50.left", {"start": v(50, 50) * mm, "end": v(50, -50) * mm});
            skLineSegment(sketch, "E50.right", {"start": v(-50, 50) * mm, "end": v(-50, -50) * mm});
            skPoint(sketch, "E50.middle", {"position": v(0, 0) * mm});
            skLineSegment(sketch, "E51", {"start": v(-50, -50) * mm, "end": v(-50, -55) * mm});
            skLineSegment(sketch, "E52", {"start": v(-50, -55) * mm, "end": v(50, -55) * mm});
            skLineSegment(sketch, "E53", {"start": v(50, -55) * mm, "end": v(50, -50) * mm});
            skSolve(sketch);
        }
        {
            var Q0;
            Q0 = qSketchRegion(id + "F2", true);
            extrude(context, id + "F3", {"entities" : qUnion([Q0]), "operationType" : NewBodyOperationType.ADD, "depth" : 10 * mm, "offsetDistance" : 25 * mm});
        }
        {
            var Q0;
            Q0=qCreatedBy(makeId("Top.planeOp"),FACE);
            var sketch = newSketch(context, id + "F4", { "sketchPlane" : qUnion([Q0])});
            skLineSegment(sketch, "E54", {"start": v(0, 0) * mm, "end": v(189.8, 0) * mm});
            skLineSegment(sketch, "E55.bottom", {"start": v(0, 0) * mm, "end": v(1.6, 0) * mm});
            skLineSegment(sketch, "E55.top", {"start": v(0, -100) * mm, "end": v(1.6, -100) * mm});
            skLineSegment(sketch, "E55.left", {"start": v(0, 0) * mm, "end": v(0, -100) * mm});
            skLineSegment(sketch, "E55.right", {"start": v(1.6, 0) * mm, "end": v(1.6, -100) * mm});
            skLineSegment(sketch, "E56", {"start": v(1.6, 0) * mm, "end": v(11.6, 0) * mm});
            skLineSegment(sketch, "E57.bottom", {"start": v(11.6, 0) * mm, "end": v(13.25, 0) * mm});
            skLineSegment(sketch, "E57.top", {"start": v(11.6, -100) * mm, "end": v(13.25, -100) * mm});
            skLineSegment(sketch, "E57.left", {"start": v(11.6, 0) * mm, "end": v(11.6, -100) * mm});
            skLineSegment(sketch, "E57.right", {"start": v(13.25, 0) * mm, "end": v(13.25, -100) * mm});
            skLineSegment(sketch, "E58", {"start": v(13.25, 0) * mm, "end": v(23.25, 0) * mm});
            skLineSegment(sketch, "E59.bottom", {"start": v(23.25, 0) * mm, "end": v(24.95, 0) * mm});
            skLineSegment(sketch, "E59.top", {"start": v(23.25, -100) * mm, "end": v(24.95, -100) * mm});
            skLineSegment(sketch, "E59.left", {"start": v(23.25, 0) * mm, "end": v(23.25, -100) * mm});
            skLineSegment(sketch, "E59.right", {"start": v(24.95, 0) * mm, "end": v(24.95, -100) * mm});
            skLineSegment(sketch, "E60", {"start": v(24.95, 0) * mm, "end": v(34.95, 0) * mm});
            skLineSegment(sketch, "E61.bottom", {"start": v(34.95, 0) * mm, "end": v(36.7, 0) * mm});
            skLineSegment(sketch, "E61.top", {"start": v(34.95, -100) * mm, "end": v(36.7, -100) * mm});
            skLineSegment(sketch, "E61.left", {"start": v(34.95, 0) * mm, "end": v(34.95, -100) * mm});
            skLineSegment(sketch, "E61.right", {"start": v(36.7, 0) * mm, "end": v(36.7, -100) * mm});
            skLineSegment(sketch, "E62", {"start": v(36.7, 0) * mm, "end": v(46.7, 0) * mm});
            skLineSegment(sketch, "E63.bottom", {"start": v(46.7, 0) * mm, "end": v(48.5, 0) * mm});
            skLineSegment(sketch, "E63.top", {"start": v(46.7, -100) * mm, "end": v(48.5, -100) * mm});
            skLineSegment(sketch, "E63.left", {"start": v(46.7, 0) * mm, "end": v(46.7, -100) * mm});
            skLineSegment(sketch, "E63.right", {"start": v(48.5, 0) * mm, "end": v(48.5, -100) * mm});
            skLineSegment(sketch, "E64", {"start": v(48.5, 0) * mm, "end": v(58.5, 0) * mm});
            skLineSegment(sketch, "E65.bottom", {"start": v(58.5, 0) * mm, "end": v(60.35, 0) * mm});
            skLineSegment(sketch, "E65.top", {"start": v(58.5, -100) * mm, "end": v(60.35, -100) * mm});
            skLineSegment(sketch, "E65.left", {"start": v(58.5, 0) * mm, "end": v(58.5, -100) * mm});
            skLineSegment(sketch, "E65.right", {"start": v(60.35, 0) * mm, "end": v(60.35, -100) * mm});
            skLineSegment(sketch, "E66", {"start": v(60.35, 0) * mm, "end": v(70.35, 0) * mm});
            skLineSegment(sketch, "E67.bottom", {"start": v(70.35, 0) * mm, "end": v(72.25, 0) * mm});
            skLineSegment(sketch, "E67.top", {"start": v(70.35, -100) * mm, "end": v(72.25, -100) * mm});
            skLineSegment(sketch, "E67.left", {"start": v(70.35, 0) * mm, "end": v(70.35, -100) * mm});
            skLineSegment(sketch, "E67.right", {"start": v(72.25, 0) * mm, "end": v(72.25, -100) * mm});
            skLineSegment(sketch, "E68", {"start": v(72.25, 0) * mm, "end": v(82.25, 0) * mm});
            skLineSegment(sketch, "E69.bottom", {"start": v(82.25, 0) * mm, "end": v(84.2, 0) * mm});
            skLineSegment(sketch, "E69.top", {"start": v(82.25, -100) * mm, "end": v(84.2, -100) * mm});
            skLineSegment(sketch, "E69.left", {"start": v(82.25, 0) * mm, "end": v(82.25, -100) * mm});
            skLineSegment(sketch, "E69.right", {"start": v(84.2, 0) * mm, "end": v(84.2, -100) * mm});
            skLineSegment(sketch, "E70", {"start": v(84.2, 0) * mm, "end": v(94.2, 0) * mm});
            skLineSegment(sketch, "E71.bottom", {"start": v(94.2, 0) * mm, "end": v(96.2, 0) * mm});
            skLineSegment(sketch, "E71.top", {"start": v(94.2, -100) * mm, "end": v(96.2, -100) * mm});
            skLineSegment(sketch, "E71.left", {"start": v(94.2, 0) * mm, "end": v(94.2, -100) * mm});
            skLineSegment(sketch, "E71.right", {"start": v(96.2, 0) * mm, "end": v(96.2, -100) * mm});
            skLineSegment(sketch, "E72", {"start": v(96.2, 0) * mm, "end": v(96.2, -5) * mm});
            skLineSegment(sketch, "E73", {"start": v(96.2, -5) * mm, "end": v(0, -5) * mm});
            skLineSegment(sketch, "E74.bottom", {"start": v(3.3, -97.5) * mm, "end": v(-1.7, -97.5) * mm});
            skLineSegment(sketch, "E74.top", {"start": v(3.3, -102.5) * mm, "end": v(-1.7, -102.5) * mm});
            skLineSegment(sketch, "E74.left", {"start": v(3.3, -97.5) * mm, "end": v(3.3, -102.5) * mm});
            skLineSegment(sketch, "E74.right", {"start": v(-1.7, -97.5) * mm, "end": v(-1.7, -102.5) * mm});
            skPoint(sketch, "E74.middle", {"position": v(0.8, -100) * mm});
            skLineSegment(sketch, "E75.bottom", {"start": v(14.93, -97.5) * mm, "end": v(9.93, -97.5) * mm});
            skLineSegment(sketch, "E75.top", {"start": v(14.93, -102.5) * mm, "end": v(9.93, -102.5) * mm});
            skLineSegment(sketch, "E75.left", {"start": v(14.93, -97.5) * mm, "end": v(14.93, -102.5) * mm});
            skLineSegment(sketch, "E75.right", {"start": v(9.93, -97.5) * mm, "end": v(9.93, -102.5) * mm});
            skPoint(sketch, "E75.middle", {"position": v(12.43, -100) * mm});
            skLineSegment(sketch, "E76.bottom", {"start": v(26.6, -97.5) * mm, "end": v(21.6, -97.5) * mm});
            skLineSegment(sketch, "E76.top", {"start": v(26.6, -102.5) * mm, "end": v(21.6, -102.5) * mm});
            skLineSegment(sketch, "E76.left", {"start": v(26.6, -97.5) * mm, "end": v(26.6, -102.5) * mm});
            skLineSegment(sketch, "E76.right", {"start": v(21.6, -97.5) * mm, "end": v(21.6, -102.5) * mm});
            skPoint(sketch, "E76.middle", {"position": v(24.1, -100) * mm});
            skLineSegment(sketch, "E77.bottom", {"start": v(38.33, -97.5) * mm, "end": v(33.33, -97.5) * mm});
            skLineSegment(sketch, "E77.top", {"start": v(38.33, -102.5) * mm, "end": v(33.33, -102.5) * mm});
            skLineSegment(sketch, "E77.left", {"start": v(38.33, -97.5) * mm, "end": v(38.33, -102.5) * mm});
            skLineSegment(sketch, "E77.right", {"start": v(33.33, -97.5) * mm, "end": v(33.33, -102.5) * mm});
            skPoint(sketch, "E77.middle", {"position": v(35.83, -100) * mm});
            skLineSegment(sketch, "E78.bottom", {"start": v(50.1, -97.5) * mm, "end": v(45.1, -97.5) * mm});
            skLineSegment(sketch, "E78.top", {"start": v(50.1, -102.5) * mm, "end": v(45.1, -102.5) * mm});
            skLineSegment(sketch, "E78.left", {"start": v(50.1, -97.5) * mm, "end": v(50.1, -102.5) * mm});
            skLineSegment(sketch, "E78.right", {"start": v(45.1, -97.5) * mm, "end": v(45.1, -102.5) * mm});
            skPoint(sketch, "E78.middle", {"position": v(47.6, -100) * mm});
            skLineSegment(sketch, "E79.bottom", {"start": v(61.93, -97.5) * mm, "end": v(56.93, -97.5) * mm});
            skLineSegment(sketch, "E79.top", {"start": v(61.93, -102.5) * mm, "end": v(56.93, -102.5) * mm});
            skLineSegment(sketch, "E79.left", {"start": v(61.93, -97.5) * mm, "end": v(61.93, -102.5) * mm});
            skLineSegment(sketch, "E79.right", {"start": v(56.93, -97.5) * mm, "end": v(56.93, -102.5) * mm});
            skPoint(sketch, "E79.middle", {"position": v(59.43, -100) * mm});
            skLineSegment(sketch, "E80.bottom", {"start": v(68.8, -97.5) * mm, "end": v(73.8, -97.5) * mm});
            skLineSegment(sketch, "E80.top", {"start": v(68.8, -102.5) * mm, "end": v(73.8, -102.5) * mm});
            skLineSegment(sketch, "E80.left", {"start": v(68.8, -97.5) * mm, "end": v(68.8, -102.5) * mm});
            skLineSegment(sketch, "E80.right", {"start": v(73.8, -97.5) * mm, "end": v(73.8, -102.5) * mm});
            skPoint(sketch, "E80.middle", {"position": v(71.3, -100) * mm});
            skLineSegment(sketch, "E81.bottom", {"start": v(85.73, -97.5) * mm, "end": v(80.73, -97.5) * mm});
            skLineSegment(sketch, "E81.top", {"start": v(85.73, -102.5) * mm, "end": v(80.73, -102.5) * mm});
            skLineSegment(sketch, "E81.left", {"start": v(85.73, -97.5) * mm, "end": v(85.73, -102.5) * mm});
            skLineSegment(sketch, "E81.right", {"start": v(80.73, -97.5) * mm, "end": v(80.73, -102.5) * mm});
            skPoint(sketch, "E81.middle", {"position": v(83.22, -100) * mm});
            skLineSegment(sketch, "E82.bottom", {"start": v(92.7, -97.5) * mm, "end": v(97.7, -97.5) * mm});
            skLineSegment(sketch, "E82.top", {"start": v(92.7, -102.5) * mm, "end": v(97.7, -102.5) * mm});
            skLineSegment(sketch, "E82.left", {"start": v(92.7, -97.5) * mm, "end": v(92.7, -102.5) * mm});
            skLineSegment(sketch, "E82.right", {"start": v(97.7, -97.5) * mm, "end": v(97.7, -102.5) * mm});
            skPoint(sketch, "E82.middle", {"position": v(95.2, -100) * mm});
            skSolve(sketch);
        }
        {
            var Q0;
            Q0 = qSketchRegion(id + "F4", true);
            extrude(context, id + "F5", {"entities" : qUnion([Q0]), "depth" : 15 * mm, "offsetDistance" : 25 * mm});
        }
        {
            var Q0;
            Q0=makeQuery(id+"F5.opExtrude","SWEPT_EDGE",EDGE,{"disambiguationData":[OSD([sQuery(id+"F4.wireOp",EDGE,"E82.top"),sQuery(id+"F4.wireOp",EDGE,"E82.right")])]});
            var Q1;
            Q1=makeQuery(id+"F5.opExtrude","SWEPT_EDGE",EDGE,{"disambiguationData":[OSD([sQuery(id+"F4.wireOp",EDGE,"E82.top"),sQuery(id+"F4.wireOp",EDGE,"E82.left")])]});
            var Q2;
            Q2=makeQuery(id+"F5.opExtrude","SWEPT_EDGE",EDGE,{"disambiguationData":[OSD([sQuery(id+"F4.wireOp",EDGE,"E81.top"),sQuery(id+"F4.wireOp",EDGE,"E81.left")])]});
            var Q3;
            Q3=makeQuery(id+"F5.opExtrude","SWEPT_EDGE",EDGE,{"disambiguationData":[OSD([sQuery(id+"F4.wireOp",EDGE,"E81.top"),sQuery(id+"F4.wireOp",EDGE,"E81.right")])]});
            var Q4;
            Q4=makeQuery(id+"F5.opExtrude","SWEPT_EDGE",EDGE,{"disambiguationData":[OSD([sQuery(id+"F4.wireOp",EDGE,"E80.top"),sQuery(id+"F4.wireOp",EDGE,"E80.right")])]});
            var Q5;
            Q5=makeQuery(id+"F5.opExtrude","SWEPT_EDGE",EDGE,{"disambiguationData":[OSD([sQuery(id+"F4.wireOp",EDGE,"E80.top"),sQuery(id+"F4.wireOp",EDGE,"E80.left")])]});
            var Q6;
            Q6=makeQuery(id+"F5.opExtrude","SWEPT_EDGE",EDGE,{"disambiguationData":[OSD([sQuery(id+"F4.wireOp",EDGE,"E79.top"),sQuery(id+"F4.wireOp",EDGE,"E79.left")])]});
            var Q7;
            Q7=makeQuery(id+"F5.opExtrude","SWEPT_EDGE",EDGE,{"disambiguationData":[OSD([sQuery(id+"F4.wireOp",EDGE,"E79.top"),sQuery(id+"F4.wireOp",EDGE,"E79.right")])]});
            var Q8;
            Q8=makeQuery(id+"F5.opExtrude","SWEPT_EDGE",EDGE,{"disambiguationData":[OSD([sQuery(id+"F4.wireOp",EDGE,"E78.top"),sQuery(id+"F4.wireOp",EDGE,"E78.left")])]});
            var Q9;
            Q9=makeQuery(id+"F5.opExtrude","SWEPT_EDGE",EDGE,{"disambiguationData":[OSD([sQuery(id+"F4.wireOp",EDGE,"E78.top"),sQuery(id+"F4.wireOp",EDGE,"E78.right")])]});
            var Q10;
            Q10=makeQuery(id+"F5.opExtrude","SWEPT_EDGE",EDGE,{"disambiguationData":[OSD([sQuery(id+"F4.wireOp",EDGE,"E77.top"),sQuery(id+"F4.wireOp",EDGE,"E77.left")])]});
            var Q11;
            Q11=makeQuery(id+"F5.opExtrude","SWEPT_EDGE",EDGE,{"disambiguationData":[OSD([sQuery(id+"F4.wireOp",EDGE,"E77.top"),sQuery(id+"F4.wireOp",EDGE,"E77.right")])]});
            var Q12;
            Q12=makeQuery(id+"F5.opExtrude","SWEPT_EDGE",EDGE,{"disambiguationData":[OSD([sQuery(id+"F4.wireOp",EDGE,"E76.top"),sQuery(id+"F4.wireOp",EDGE,"E76.left")])]});
            var Q13;
            Q13=makeQuery(id+"F5.opExtrude","SWEPT_EDGE",EDGE,{"disambiguationData":[OSD([sQuery(id+"F4.wireOp",EDGE,"E76.top"),sQuery(id+"F4.wireOp",EDGE,"E76.right")])]});
            var Q14;
            Q14=makeQuery(id+"F5.opExtrude","SWEPT_EDGE",EDGE,{"disambiguationData":[OSD([sQuery(id+"F4.wireOp",EDGE,"E75.top"),sQuery(id+"F4.wireOp",EDGE,"E75.left")])]});
            var Q15;
            Q15=makeQuery(id+"F5.opExtrude","SWEPT_EDGE",EDGE,{"disambiguationData":[OSD([sQuery(id+"F4.wireOp",EDGE,"E75.top"),sQuery(id+"F4.wireOp",EDGE,"E75.right")])]});
            var Q16;
            Q16=makeQuery(id+"F5.opExtrude","SWEPT_EDGE",EDGE,{"disambiguationData":[OSD([sQuery(id+"F4.wireOp",EDGE,"E74.top"),sQuery(id+"F4.wireOp",EDGE,"E74.left")])]});
            var Q17;
            Q17=makeQuery(id+"F5.opExtrude","SWEPT_EDGE",EDGE,{"disambiguationData":[OSD([sQuery(id+"F4.wireOp",EDGE,"E74.top"),sQuery(id+"F4.wireOp",EDGE,"E74.right")])]});
            var Q18;
            Q18=makeQuery(id+"F5.opExtrude","SWEPT_EDGE",EDGE,{"disambiguationData":[OSD([sQuery(id+"F4.wireOp",EDGE,"E54"),sQuery(id+"F4.wireOp",EDGE,"E55.left")])]});
            var Q19;
            Q19=makeQuery(id+"F5.opExtrude","SWEPT_EDGE",EDGE,{"disambiguationData":[OSD([sQuery(id+"F4.wireOp",EDGE,"E54"),sQuery(id+"F4.wireOp",EDGE,"E71.right")])]});
            fillet(context, id + "F6", {"entities" : qUnion([Q0, Q1, Q2, Q3, Q4, Q5, Q6, Q7, Q8, Q9, Q10, Q11, Q12, Q13, Q14, Q15, Q16, Q17, Q18, Q19]), "tangentPropagation" : true, "radius" : 2.5 * mm, "defaultsChanged" : false, "vertexSettings" : [], "allowEdgeOverflow" : false});
        }
        {
            var Q0;
            Q0=makeQuery(id+"F5.opExtrude","SWEPT_EDGE",EDGE,{"disambiguationData":[OSD([sQuery(id+"F4.wireOp",EDGE,"E71.left"),sQuery(id+"F4.wireOp",EDGE,"E73")])]});
            var Q1;
            Q1=makeQuery(id+"F5.opExtrude","SWEPT_EDGE",EDGE,{"disambiguationData":[OSD([sQuery(id+"F4.wireOp",EDGE,"E69.left"),sQuery(id+"F4.wireOp",EDGE,"E73")])]});
            var Q2;
            Q2=makeQuery(id+"F5.opExtrude","SWEPT_EDGE",EDGE,{"disambiguationData":[OSD([sQuery(id+"F4.wireOp",EDGE,"E67.left"),sQuery(id+"F4.wireOp",EDGE,"E73")])]});
            var Q3;
            Q3=makeQuery(id+"F5.opExtrude","SWEPT_EDGE",EDGE,{"disambiguationData":[OSD([sQuery(id+"F4.wireOp",EDGE,"E65.left"),sQuery(id+"F4.wireOp",EDGE,"E73")])]});
            var Q4;
            Q4=makeQuery(id+"F5.opExtrude","SWEPT_EDGE",EDGE,{"disambiguationData":[OSD([sQuery(id+"F4.wireOp",EDGE,"E63.left"),sQuery(id+"F4.wireOp",EDGE,"E73")])]});
            var Q5;
            Q5=makeQuery(id+"F5.opExtrude","SWEPT_EDGE",EDGE,{"disambiguationData":[OSD([sQuery(id+"F4.wireOp",EDGE,"E61.left"),sQuery(id+"F4.wireOp",EDGE,"E73")])]});
            var Q6;
            Q6=makeQuery(id+"F5.opExtrude","SWEPT_EDGE",EDGE,{"disambiguationData":[OSD([sQuery(id+"F4.wireOp",EDGE,"E59.left"),sQuery(id+"F4.wireOp",EDGE,"E73")])]});
            var Q7;
            Q7=makeQuery(id+"F5.opExtrude","SWEPT_EDGE",EDGE,{"disambiguationData":[OSD([sQuery(id+"F4.wireOp",EDGE,"E57.left"),sQuery(id+"F4.wireOp",EDGE,"E73")])]});
            var Q8;
            Q8=makeQuery(id+"F5.opExtrude","SWEPT_EDGE",EDGE,{"disambiguationData":[OSD([sQuery(id+"F4.wireOp",EDGE,"E55.right"),sQuery(id+"F4.wireOp",EDGE,"E73")])]});
            var Q9;
            Q9=makeQuery(id+"F5.opExtrude","SWEPT_EDGE",EDGE,{"disambiguationData":[OSD([sQuery(id+"F4.wireOp",EDGE,"E57.right"),sQuery(id+"F4.wireOp",EDGE,"E73")])]});
            var Q10;
            Q10=makeQuery(id+"F5.opExtrude","SWEPT_EDGE",EDGE,{"disambiguationData":[OSD([sQuery(id+"F4.wireOp",EDGE,"E59.right"),sQuery(id+"F4.wireOp",EDGE,"E73")])]});
            var Q11;
            Q11=makeQuery(id+"F5.opExtrude","SWEPT_EDGE",EDGE,{"disambiguationData":[OSD([sQuery(id+"F4.wireOp",EDGE,"E61.right"),sQuery(id+"F4.wireOp",EDGE,"E73")])]});
            var Q12;
            Q12=makeQuery(id+"F5.opExtrude","SWEPT_EDGE",EDGE,{"disambiguationData":[OSD([sQuery(id+"F4.wireOp",EDGE,"E63.right"),sQuery(id+"F4.wireOp",EDGE,"E73")])]});
            var Q13;
            Q13=makeQuery(id+"F5.opExtrude","SWEPT_EDGE",EDGE,{"disambiguationData":[OSD([sQuery(id+"F4.wireOp",EDGE,"E65.right"),sQuery(id+"F4.wireOp",EDGE,"E73")])]});
            var Q14;
            Q14=makeQuery(id+"F5.opExtrude","SWEPT_EDGE",EDGE,{"disambiguationData":[OSD([sQuery(id+"F4.wireOp",EDGE,"E67.right"),sQuery(id+"F4.wireOp",EDGE,"E73")])]});
            var Q15;
            Q15=makeQuery(id+"F5.opExtrude","SWEPT_EDGE",EDGE,{"disambiguationData":[OSD([sQuery(id+"F4.wireOp",EDGE,"E69.right"),sQuery(id+"F4.wireOp",EDGE,"E73")])]});
            fillet(context, id + "F7", {"entities" : qUnion([Q0, Q1, Q2, Q3, Q4, Q5, Q6, Q7, Q8, Q9, Q10, Q11, Q12, Q13, Q14, Q15]), "tangentPropagation" : true, "radius" : 5 * mm, "defaultsChanged" : false, "vertexSettings" : [], "allowEdgeOverflow" : false});
        }
        {
            var Q0;
            Q0=makeQuery(id+"F5.opExtrude","SWEPT_EDGE",EDGE,{"disambiguationData":[OSD([sQuery(id+"F4.wireOp",EDGE,"E82.bottom"),sQuery(id+"F4.wireOp",EDGE,"E82.right")])]});
            var Q1;
            Q1=makeQuery(id+"F5.opExtrude","SWEPT_EDGE",EDGE,{"disambiguationData":[OSD([sQuery(id+"F4.wireOp",EDGE,"E71.right"),sQuery(id+"F4.wireOp",EDGE,"E82.bottom")])]});
            var Q2;
            Q2=makeQuery(id+"F5.opExtrude","SWEPT_EDGE",EDGE,{"disambiguationData":[OSD([sQuery(id+"F4.wireOp",EDGE,"E71.left"),sQuery(id+"F4.wireOp",EDGE,"E82.bottom")])]});
            var Q3;
            Q3=makeQuery(id+"F5.opExtrude","SWEPT_EDGE",EDGE,{"disambiguationData":[OSD([sQuery(id+"F4.wireOp",EDGE,"E82.bottom"),sQuery(id+"F4.wireOp",EDGE,"E82.left")])]});
            var Q4;
            Q4=makeQuery(id+"F5.opExtrude","SWEPT_EDGE",EDGE,{"disambiguationData":[OSD([sQuery(id+"F4.wireOp",EDGE,"E81.bottom"),sQuery(id+"F4.wireOp",EDGE,"E81.left")])]});
            var Q5;
            Q5=makeQuery(id+"F5.opExtrude","SWEPT_EDGE",EDGE,{"disambiguationData":[OSD([sQuery(id+"F4.wireOp",EDGE,"E69.right"),sQuery(id+"F4.wireOp",EDGE,"E81.bottom")])]});
            var Q6;
            Q6=makeQuery(id+"F5.opExtrude","SWEPT_EDGE",EDGE,{"disambiguationData":[OSD([sQuery(id+"F4.wireOp",EDGE,"E81.bottom"),sQuery(id+"F4.wireOp",EDGE,"E81.right")])]});
            var Q7;
            Q7=makeQuery(id+"F5.opExtrude","SWEPT_EDGE",EDGE,{"disambiguationData":[OSD([sQuery(id+"F4.wireOp",EDGE,"E69.left"),sQuery(id+"F4.wireOp",EDGE,"E81.bottom")])]});
            var Q8;
            Q8=makeQuery(id+"F5.opExtrude","SWEPT_EDGE",EDGE,{"disambiguationData":[OSD([sQuery(id+"F4.wireOp",EDGE,"E80.bottom"),sQuery(id+"F4.wireOp",EDGE,"E80.right")])]});
            var Q9;
            Q9=makeQuery(id+"F5.opExtrude","SWEPT_EDGE",EDGE,{"disambiguationData":[OSD([sQuery(id+"F4.wireOp",EDGE,"E67.right"),sQuery(id+"F4.wireOp",EDGE,"E80.bottom")])]});
            var Q10;
            Q10=makeQuery(id+"F5.opExtrude","SWEPT_EDGE",EDGE,{"disambiguationData":[OSD([sQuery(id+"F4.wireOp",EDGE,"E67.left"),sQuery(id+"F4.wireOp",EDGE,"E80.bottom")])]});
            var Q11;
            Q11=makeQuery(id+"F5.opExtrude","SWEPT_EDGE",EDGE,{"disambiguationData":[OSD([sQuery(id+"F4.wireOp",EDGE,"E80.bottom"),sQuery(id+"F4.wireOp",EDGE,"E80.left")])]});
            var Q12;
            Q12=makeQuery(id+"F5.opExtrude","SWEPT_EDGE",EDGE,{"disambiguationData":[OSD([sQuery(id+"F4.wireOp",EDGE,"E79.bottom"),sQuery(id+"F4.wireOp",EDGE,"E79.right")])]});
            var Q13;
            Q13=makeQuery(id+"F5.opExtrude","SWEPT_EDGE",EDGE,{"disambiguationData":[OSD([sQuery(id+"F4.wireOp",EDGE,"E65.left"),sQuery(id+"F4.wireOp",EDGE,"E79.bottom")])]});
            var Q14;
            Q14=makeQuery(id+"F5.opExtrude","SWEPT_EDGE",EDGE,{"disambiguationData":[OSD([sQuery(id+"F4.wireOp",EDGE,"E65.right"),sQuery(id+"F4.wireOp",EDGE,"E79.bottom")])]});
            var Q15;
            Q15=makeQuery(id+"F5.opExtrude","SWEPT_EDGE",EDGE,{"disambiguationData":[OSD([sQuery(id+"F4.wireOp",EDGE,"E79.bottom"),sQuery(id+"F4.wireOp",EDGE,"E79.left")])]});
            var Q16;
            Q16=makeQuery(id+"F5.opExtrude","SWEPT_EDGE",EDGE,{"disambiguationData":[OSD([sQuery(id+"F4.wireOp",EDGE,"E78.bottom"),sQuery(id+"F4.wireOp",EDGE,"E78.left")])]});
            var Q17;
            Q17=makeQuery(id+"F5.opExtrude","SWEPT_EDGE",EDGE,{"disambiguationData":[OSD([sQuery(id+"F4.wireOp",EDGE,"E63.right"),sQuery(id+"F4.wireOp",EDGE,"E78.bottom")])]});
            var Q18;
            Q18=makeQuery(id+"F5.opExtrude","SWEPT_EDGE",EDGE,{"disambiguationData":[OSD([sQuery(id+"F4.wireOp",EDGE,"E63.left"),sQuery(id+"F4.wireOp",EDGE,"E78.bottom")])]});
            var Q19;
            Q19=makeQuery(id+"F5.opExtrude","SWEPT_EDGE",EDGE,{"disambiguationData":[OSD([sQuery(id+"F4.wireOp",EDGE,"E78.bottom"),sQuery(id+"F4.wireOp",EDGE,"E78.right")])]});
            var Q20;
            Q20=makeQuery(id+"F5.opExtrude","SWEPT_EDGE",EDGE,{"disambiguationData":[OSD([sQuery(id+"F4.wireOp",EDGE,"E61.left"),sQuery(id+"F4.wireOp",EDGE,"E77.bottom")])]});
            var Q21;
            Q21=makeQuery(id+"F5.opExtrude","SWEPT_EDGE",EDGE,{"disambiguationData":[OSD([sQuery(id+"F4.wireOp",EDGE,"E77.bottom"),sQuery(id+"F4.wireOp",EDGE,"E77.right")])]});
            var Q22;
            Q22=makeQuery(id+"F5.opExtrude","SWEPT_EDGE",EDGE,{"disambiguationData":[OSD([sQuery(id+"F4.wireOp",EDGE,"E77.bottom"),sQuery(id+"F4.wireOp",EDGE,"E77.left")])]});
            var Q23;
            Q23=makeQuery(id+"F5.opExtrude","SWEPT_EDGE",EDGE,{"disambiguationData":[OSD([sQuery(id+"F4.wireOp",EDGE,"E61.right"),sQuery(id+"F4.wireOp",EDGE,"E77.bottom")])]});
            var Q24;
            Q24=makeQuery(id+"F5.opExtrude","SWEPT_EDGE",EDGE,{"disambiguationData":[OSD([sQuery(id+"F4.wireOp",EDGE,"E76.bottom"),sQuery(id+"F4.wireOp",EDGE,"E76.left")])]});
            var Q25;
            Q25=makeQuery(id+"F5.opExtrude","SWEPT_EDGE",EDGE,{"disambiguationData":[OSD([sQuery(id+"F4.wireOp",EDGE,"E59.right"),sQuery(id+"F4.wireOp",EDGE,"E76.bottom")])]});
            var Q26;
            Q26=makeQuery(id+"F5.opExtrude","SWEPT_EDGE",EDGE,{"disambiguationData":[OSD([sQuery(id+"F4.wireOp",EDGE,"E59.left"),sQuery(id+"F4.wireOp",EDGE,"E76.bottom")])]});
            var Q27;
            Q27=makeQuery(id+"F5.opExtrude","SWEPT_EDGE",EDGE,{"disambiguationData":[OSD([sQuery(id+"F4.wireOp",EDGE,"E76.bottom"),sQuery(id+"F4.wireOp",EDGE,"E76.right")])]});
            var Q28;
            Q28=makeQuery(id+"F5.opExtrude","SWEPT_EDGE",EDGE,{"disambiguationData":[OSD([sQuery(id+"F4.wireOp",EDGE,"E75.bottom"),sQuery(id+"F4.wireOp",EDGE,"E75.right")])]});
            var Q29;
            Q29=makeQuery(id+"F5.opExtrude","SWEPT_EDGE",EDGE,{"disambiguationData":[OSD([sQuery(id+"F4.wireOp",EDGE,"E57.left"),sQuery(id+"F4.wireOp",EDGE,"E75.bottom")])]});
            var Q30;
            Q30=makeQuery(id+"F5.opExtrude","SWEPT_EDGE",EDGE,{"disambiguationData":[OSD([sQuery(id+"F4.wireOp",EDGE,"E55.left"),sQuery(id+"F4.wireOp",EDGE,"E74.bottom")])]});
            var Q31;
            Q31=makeQuery(id+"F5.opExtrude","SWEPT_EDGE",EDGE,{"disambiguationData":[OSD([sQuery(id+"F4.wireOp",EDGE,"E74.bottom"),sQuery(id+"F4.wireOp",EDGE,"E74.right")])]});
            var Q32;
            Q32=makeQuery(id+"F5.opExtrude","SWEPT_EDGE",EDGE,{"disambiguationData":[OSD([sQuery(id+"F4.wireOp",EDGE,"E55.right"),sQuery(id+"F4.wireOp",EDGE,"E74.bottom")])]});
            var Q33;
            Q33=makeQuery(id+"F5.opExtrude","SWEPT_EDGE",EDGE,{"disambiguationData":[OSD([sQuery(id+"F4.wireOp",EDGE,"E74.bottom"),sQuery(id+"F4.wireOp",EDGE,"E74.left")])]});
            var Q34;
            Q34=makeQuery(id+"F5.opExtrude","SWEPT_EDGE",EDGE,{"disambiguationData":[OSD([sQuery(id+"F4.wireOp",EDGE,"E57.right"),sQuery(id+"F4.wireOp",EDGE,"E75.bottom")])]});
            var Q35;
            Q35=makeQuery(id+"F5.opExtrude","SWEPT_EDGE",EDGE,{"disambiguationData":[OSD([sQuery(id+"F4.wireOp",EDGE,"E75.bottom"),sQuery(id+"F4.wireOp",EDGE,"E75.left")])]});
            fillet(context, id + "F8", {"entities" : qUnion([Q0, Q1, Q2, Q3, Q4, Q5, Q6, Q7, Q8, Q9, Q10, Q11, Q12, Q13, Q14, Q15, Q16, Q17, Q18, Q19, Q20, Q21, Q22, Q23, Q24, Q25, Q26, Q27, Q28, Q29, Q30, Q31, Q32, Q33, Q34, Q35]), "tangentPropagation" : true, "radius" : 0.75 * mm, "defaultsChanged" : false, "vertexSettings" : [], "allowEdgeOverflow" : false});
        }
    });
